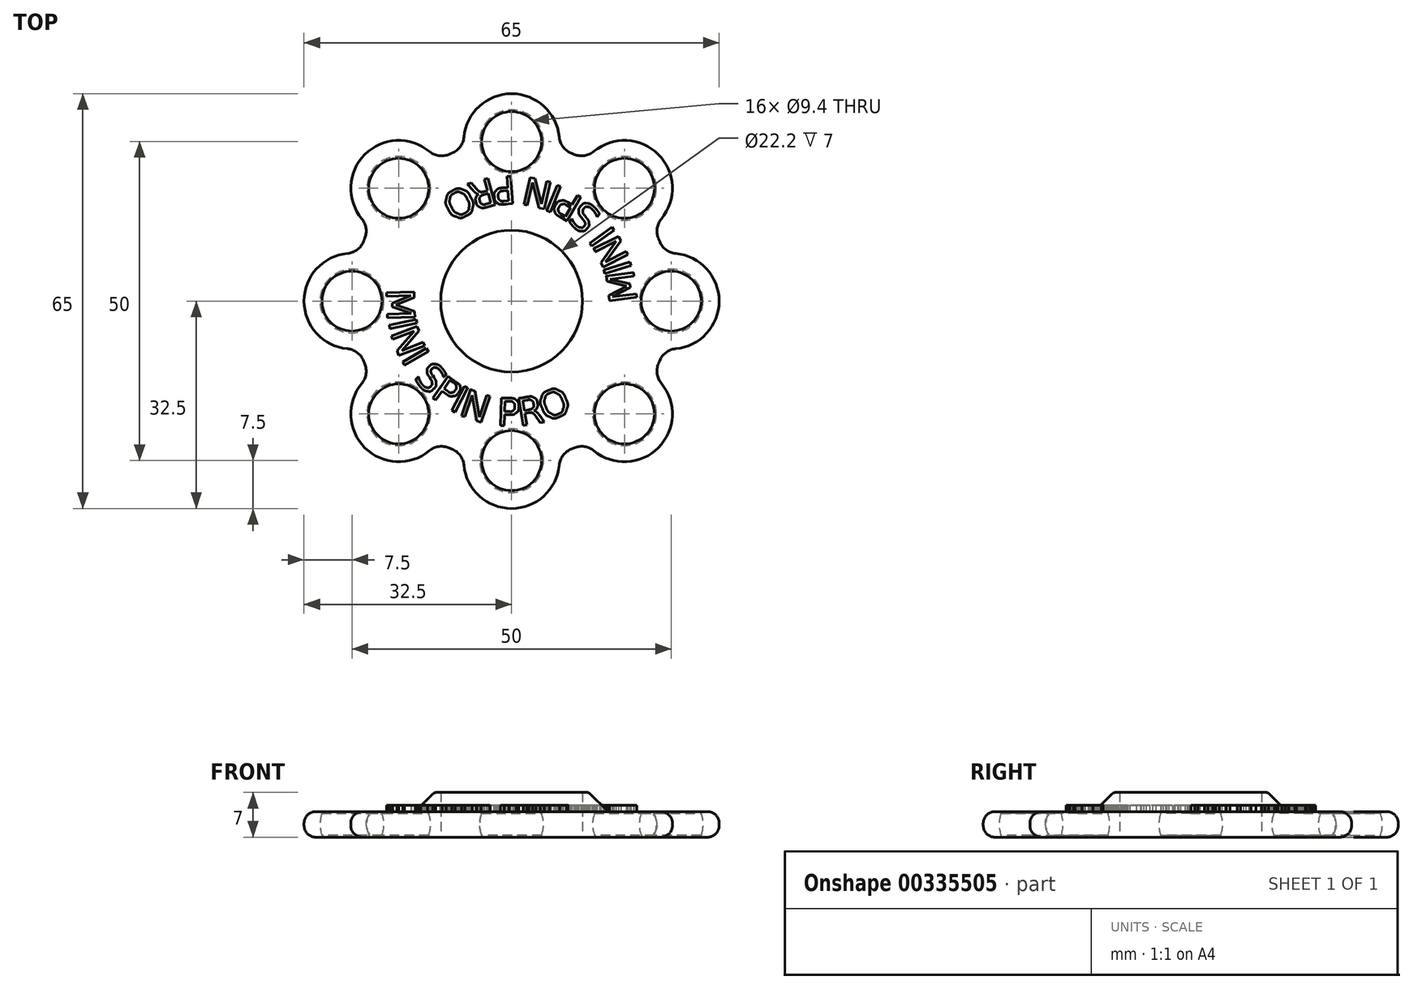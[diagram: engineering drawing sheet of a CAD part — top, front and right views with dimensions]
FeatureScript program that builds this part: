
annotation { "Feature Type Name" : "Feature", "Feature Type Description" : "" }
export const myFeature = defineFeature(function(context is Context, id is Id, definition is map)
    precondition{}
    {
        {
            var Q0;
            Q0=qCreatedBy(makeId("Top.planeOp"),FACE);
            var sketch = newSketch(context, id + "F0", { "sketchPlane" : qUnion([Q0])});
            skCircle(sketch, "E0", {"center": v(0, 0) * mm, "radius": 11.1 * mm});
            skPoint(sketch, "E1.0.midPoint", {"position": v(12.23, 6.82) * mm});
            skCircle(sketch, "E2", {"center": v(0, 25) * mm, "radius": 4.7 * mm});
            skCircle(sketch, "E3.1.0", {"center": v(-17.68, 17.68) * mm, "radius": 4.7 * mm});
            skCircle(sketch, "E3.2.0", {"center": v(-25, 0) * mm, "radius": 4.7 * mm});
            skCircle(sketch, "E3.3.0", {"center": v(-17.68, -17.68) * mm, "radius": 4.7 * mm});
            skCircle(sketch, "E3.4.0", {"center": v(0, -25) * mm, "radius": 4.7 * mm});
            skCircle(sketch, "E3.5.0", {"center": v(17.68, -17.68) * mm, "radius": 4.7 * mm});
            skCircle(sketch, "E3.6.0", {"center": v(25, 0) * mm, "radius": 4.7 * mm});
            skCircle(sketch, "E3.7.0", {"center": v(17.68, 17.68) * mm, "radius": 4.7 * mm});
            skCircle(sketch, "E4", {"center": v(0, 25) * mm, "radius": 7.5 * mm});
            skCircle(sketch, "E5.1.0", {"center": v(-17.68, 17.68) * mm, "radius": 7.5 * mm});
            skCircle(sketch, "E5.2.0", {"center": v(-25, 0) * mm, "radius": 7.5 * mm});
            skCircle(sketch, "E5.3.0", {"center": v(-17.68, -17.68) * mm, "radius": 7.5 * mm});
            skCircle(sketch, "E5.4.0", {"center": v(0, -25) * mm, "radius": 7.5 * mm});
            skCircle(sketch, "E5.5.0", {"center": v(17.68, -17.68) * mm, "radius": 7.5 * mm});
            skCircle(sketch, "E5.6.0", {"center": v(25, 0) * mm, "radius": 7.5 * mm});
            skCircle(sketch, "E5.7.0", {"center": v(17.68, 17.68) * mm, "radius": 7.5 * mm});
            skCircle(sketch, "E6", {"center": v(0, 0) * mm, "radius": 25 * mm});
            skSolve(sketch);
        }
        {
            var Q0;
            Q0=makeQuery(id+"F0.imprint","IMPRINT",FACE,{"disambiguationData":[TD([[makeQuery(id+"F0.imprint","IMPRINT",EDGE,{"derivedFrom":sQuery(id+"F0.wireOp",EDGE,"E0")}),-1.0]])]});
            var Q1;
            {var subQ0=sQuery(id+"F0.wireOp",EDGE,"E6");var subQ1=sQuery(id+"F0.wireOp",EDGE,"E3.3.0");var subQ2=makeQuery(id+"F0.imprint","INTERSECT",VERTEX,{"disambiguationData":[OD(0.0)],"derivedFrom":[subQ1,subQ0]});Q1=makeQuery(id+"F0.imprint","IMPRINT",FACE,{"disambiguationData":[TD([[makeQuery(id+"F0.imprint","IMPRINT",EDGE,{"disambiguationData":[TD([[subQ2,-1.0]])],"derivedFrom":subQ1}),-1.0]])]});}
            var Q2;
            {var subQ0=sQuery(id+"F0.wireOp",EDGE,"E6");var subQ1=sQuery(id+"F0.wireOp",EDGE,"E3.3.0");var subQ2=makeQuery(id+"F0.imprint","INTERSECT",VERTEX,{"disambiguationData":[OD(0.0)],"derivedFrom":[subQ1,subQ0]});Q2=makeQuery(id+"F0.imprint","IMPRINT",FACE,{"disambiguationData":[TD([[makeQuery(id+"F0.imprint","IMPRINT",EDGE,{"disambiguationData":[TD([[subQ2,1.0]])],"derivedFrom":subQ1}),-1.0]])]});}
            var Q3;
            {var subQ0=sQuery(id+"F0.wireOp",EDGE,"E6");var subQ1=sQuery(id+"F0.wireOp",EDGE,"E3.2.0");var subQ2=makeQuery(id+"F0.imprint","INTERSECT",VERTEX,{"disambiguationData":[OD(0.0)],"derivedFrom":[subQ1,subQ0]});Q3=makeQuery(id+"F0.imprint","IMPRINT",FACE,{"disambiguationData":[TD([[makeQuery(id+"F0.imprint","IMPRINT",EDGE,{"disambiguationData":[TD([[subQ2,1.0]])],"derivedFrom":subQ1}),-1.0]])]});}
            var Q4;
            {var subQ0=sQuery(id+"F0.wireOp",EDGE,"E6");var subQ1=sQuery(id+"F0.wireOp",EDGE,"E3.2.0");var subQ2=makeQuery(id+"F0.imprint","INTERSECT",VERTEX,{"disambiguationData":[OD(0.0)],"derivedFrom":[subQ1,subQ0]});Q4=makeQuery(id+"F0.imprint","IMPRINT",FACE,{"disambiguationData":[TD([[makeQuery(id+"F0.imprint","IMPRINT",EDGE,{"disambiguationData":[TD([[subQ2,-1.0]])],"derivedFrom":subQ1}),-1.0]])]});}
            var Q5;
            {var subQ0=sQuery(id+"F0.wireOp",EDGE,"E6");var subQ1=sQuery(id+"F0.wireOp",EDGE,"E3.1.0");var subQ2=makeQuery(id+"F0.imprint","INTERSECT",VERTEX,{"disambiguationData":[OD(0.0)],"derivedFrom":[subQ1,subQ0]});Q5=makeQuery(id+"F0.imprint","IMPRINT",FACE,{"disambiguationData":[TD([[makeQuery(id+"F0.imprint","IMPRINT",EDGE,{"disambiguationData":[TD([[subQ2,-1.0]])],"derivedFrom":subQ1}),-1.0]])]});}
            var Q6;
            {var subQ0=sQuery(id+"F0.wireOp",EDGE,"E6");var subQ1=sQuery(id+"F0.wireOp",EDGE,"E3.1.0");var subQ2=makeQuery(id+"F0.imprint","INTERSECT",VERTEX,{"disambiguationData":[OD(0.0)],"derivedFrom":[subQ1,subQ0]});Q6=makeQuery(id+"F0.imprint","IMPRINT",FACE,{"disambiguationData":[TD([[makeQuery(id+"F0.imprint","IMPRINT",EDGE,{"disambiguationData":[TD([[subQ2,1.0]])],"derivedFrom":subQ1}),-1.0]])]});}
            var Q7;
            {var subQ0=sQuery(id+"F0.wireOp",EDGE,"E6");var subQ1=sQuery(id+"F0.wireOp",EDGE,"E2");var subQ2=makeQuery(id+"F0.imprint","INTERSECT",VERTEX,{"disambiguationData":[OD(0.0)],"derivedFrom":[subQ1,subQ0]});Q7=makeQuery(id+"F0.imprint","IMPRINT",FACE,{"disambiguationData":[TD([[makeQuery(id+"F0.imprint","IMPRINT",EDGE,{"disambiguationData":[TD([[subQ2,1.0]])],"derivedFrom":subQ1}),-1.0]])]});}
            var Q8;
            {var subQ0=sQuery(id+"F0.wireOp",EDGE,"E6");var subQ1=sQuery(id+"F0.wireOp",EDGE,"E2");var subQ2=makeQuery(id+"F0.imprint","INTERSECT",VERTEX,{"disambiguationData":[OD(0.0)],"derivedFrom":[subQ1,subQ0]});Q8=makeQuery(id+"F0.imprint","IMPRINT",FACE,{"disambiguationData":[TD([[makeQuery(id+"F0.imprint","IMPRINT",EDGE,{"disambiguationData":[TD([[subQ2,-1.0]])],"derivedFrom":subQ1}),-1.0]])]});}
            var Q9;
            {var subQ0=sQuery(id+"F0.wireOp",EDGE,"E6");var subQ1=sQuery(id+"F0.wireOp",EDGE,"E3.7.0");var subQ2=makeQuery(id+"F0.imprint","INTERSECT",VERTEX,{"disambiguationData":[OD(0.0)],"derivedFrom":[subQ1,subQ0]});Q9=makeQuery(id+"F0.imprint","IMPRINT",FACE,{"disambiguationData":[TD([[makeQuery(id+"F0.imprint","IMPRINT",EDGE,{"disambiguationData":[TD([[subQ2,1.0]])],"derivedFrom":subQ1}),-1.0]])]});}
            var Q10;
            {var subQ0=sQuery(id+"F0.wireOp",EDGE,"E6");var subQ1=sQuery(id+"F0.wireOp",EDGE,"E3.7.0");var subQ2=makeQuery(id+"F0.imprint","INTERSECT",VERTEX,{"disambiguationData":[OD(0.0)],"derivedFrom":[subQ1,subQ0]});Q10=makeQuery(id+"F0.imprint","IMPRINT",FACE,{"disambiguationData":[TD([[makeQuery(id+"F0.imprint","IMPRINT",EDGE,{"disambiguationData":[TD([[subQ2,-1.0]])],"derivedFrom":subQ1}),-1.0]])]});}
            var Q11;
            {var subQ0=sQuery(id+"F0.wireOp",EDGE,"E6");var subQ1=sQuery(id+"F0.wireOp",EDGE,"E3.6.0");var subQ2=makeQuery(id+"F0.imprint","INTERSECT",VERTEX,{"disambiguationData":[OD(0.0)],"derivedFrom":[subQ1,subQ0]});Q11=makeQuery(id+"F0.imprint","IMPRINT",FACE,{"disambiguationData":[TD([[makeQuery(id+"F0.imprint","IMPRINT",EDGE,{"disambiguationData":[TD([[subQ2,-1.0]])],"derivedFrom":subQ1}),-1.0]])]});}
            var Q12;
            {var subQ0=sQuery(id+"F0.wireOp",EDGE,"E6");var subQ1=sQuery(id+"F0.wireOp",EDGE,"E3.6.0");var subQ2=makeQuery(id+"F0.imprint","INTERSECT",VERTEX,{"disambiguationData":[OD(0.0)],"derivedFrom":[subQ1,subQ0]});Q12=makeQuery(id+"F0.imprint","IMPRINT",FACE,{"disambiguationData":[TD([[makeQuery(id+"F0.imprint","IMPRINT",EDGE,{"disambiguationData":[TD([[subQ2,1.0]])],"derivedFrom":subQ1}),-1.0]])]});}
            var Q13;
            {var subQ0=sQuery(id+"F0.wireOp",EDGE,"E6");var subQ1=sQuery(id+"F0.wireOp",EDGE,"E3.5.0");var subQ2=makeQuery(id+"F0.imprint","INTERSECT",VERTEX,{"disambiguationData":[OD(0.0)],"derivedFrom":[subQ1,subQ0]});Q13=makeQuery(id+"F0.imprint","IMPRINT",FACE,{"disambiguationData":[TD([[makeQuery(id+"F0.imprint","IMPRINT",EDGE,{"disambiguationData":[TD([[subQ2,1.0]])],"derivedFrom":subQ1}),-1.0]])]});}
            var Q14;
            {var subQ0=sQuery(id+"F0.wireOp",EDGE,"E6");var subQ1=sQuery(id+"F0.wireOp",EDGE,"E3.5.0");var subQ2=makeQuery(id+"F0.imprint","INTERSECT",VERTEX,{"disambiguationData":[OD(0.0)],"derivedFrom":[subQ1,subQ0]});Q14=makeQuery(id+"F0.imprint","IMPRINT",FACE,{"disambiguationData":[TD([[makeQuery(id+"F0.imprint","IMPRINT",EDGE,{"disambiguationData":[TD([[subQ2,-1.0]])],"derivedFrom":subQ1}),-1.0]])]});}
            var Q15;
            {var subQ0=sQuery(id+"F0.wireOp",EDGE,"E6");var subQ1=sQuery(id+"F0.wireOp",EDGE,"E3.4.0");var subQ2=makeQuery(id+"F0.imprint","INTERSECT",VERTEX,{"disambiguationData":[OD(0.0)],"derivedFrom":[subQ1,subQ0]});Q15=makeQuery(id+"F0.imprint","IMPRINT",FACE,{"disambiguationData":[TD([[makeQuery(id+"F0.imprint","IMPRINT",EDGE,{"disambiguationData":[TD([[subQ2,1.0]])],"derivedFrom":subQ1}),-1.0]])]});}
            var Q16;
            {var subQ0=sQuery(id+"F0.wireOp",EDGE,"E6");var subQ1=sQuery(id+"F0.wireOp",EDGE,"E3.4.0");var subQ2=makeQuery(id+"F0.imprint","INTERSECT",VERTEX,{"disambiguationData":[OD(0.0)],"derivedFrom":[subQ1,subQ0]});Q16=makeQuery(id+"F0.imprint","IMPRINT",FACE,{"disambiguationData":[TD([[makeQuery(id+"F0.imprint","IMPRINT",EDGE,{"disambiguationData":[TD([[subQ2,-1.0]])],"derivedFrom":subQ1}),-1.0]])]});}
            extrude(context, id + "F1", {"entities" : qUnion([Q0, Q1, Q2, Q3, Q4, Q5, Q6, Q7, Q8, Q9, Q10, Q11, Q12, Q13, Q14, Q15, Q16]), "depth" : 2 * mm, "hasSecondDirection" : true, "secondDirectionOppositeDirection" : true, "secondDirectionDepth" : 2 * mm});
        }
        {
            var Q0;
            {var subQ0=sQuery(id+"F0.wireOp",EDGE,"E6");var subQ1=sQuery(id+"F0.wireOp",EDGE,"E5.4.0");Q0=makeQuery(id+"F1.opExtrude","SWEPT_EDGE",EDGE,{"disambiguationData":[OSD([subQ1,subQ0]),TDD([makeQuery(id+"F0.imprint","INTERSECT",VERTEX,{"disambiguationData":[OD(0.0)],"derivedFrom":[subQ1,subQ0]})])]});}
            var Q1;
            {var subQ0=sQuery(id+"F0.wireOp",EDGE,"E6");var subQ1=sQuery(id+"F0.wireOp",EDGE,"E5.2.0");Q1=makeQuery(id+"F1.opExtrude","SWEPT_EDGE",EDGE,{"disambiguationData":[OSD([subQ1,subQ0]),TDD([makeQuery(id+"F0.imprint","INTERSECT",VERTEX,{"disambiguationData":[OD(1.0)],"derivedFrom":[subQ1,subQ0]})])]});}
            var Q2;
            {var subQ0=sQuery(id+"F0.wireOp",EDGE,"E6");var subQ1=sQuery(id+"F0.wireOp",EDGE,"E5.2.0");Q2=makeQuery(id+"F1.opExtrude","SWEPT_EDGE",EDGE,{"disambiguationData":[OSD([subQ1,subQ0]),TDD([makeQuery(id+"F0.imprint","INTERSECT",VERTEX,{"disambiguationData":[OD(0.0)],"derivedFrom":[subQ1,subQ0]})])]});}
            var Q3;
            {var subQ0=sQuery(id+"F0.wireOp",EDGE,"E6");var subQ1=sQuery(id+"F0.wireOp",EDGE,"E4");Q3=makeQuery(id+"F1.opExtrude","SWEPT_EDGE",EDGE,{"disambiguationData":[OSD([subQ1,subQ0]),TDD([makeQuery(id+"F0.imprint","INTERSECT",VERTEX,{"disambiguationData":[OD(1.0)],"derivedFrom":[subQ1,subQ0]})])]});}
            var Q4;
            {var subQ0=sQuery(id+"F0.wireOp",EDGE,"E6");var subQ1=sQuery(id+"F0.wireOp",EDGE,"E5.7.0");Q4=makeQuery(id+"F1.opExtrude","SWEPT_EDGE",EDGE,{"disambiguationData":[OSD([subQ1,subQ0]),TDD([makeQuery(id+"F0.imprint","INTERSECT",VERTEX,{"disambiguationData":[OD(1.0)],"derivedFrom":[subQ1,subQ0]})])]});}
            var Q5;
            {var subQ0=sQuery(id+"F0.wireOp",EDGE,"E6");var subQ1=sQuery(id+"F0.wireOp",EDGE,"E5.1.0");Q5=makeQuery(id+"F1.opExtrude","SWEPT_EDGE",EDGE,{"disambiguationData":[OSD([subQ1,subQ0]),TDD([makeQuery(id+"F0.imprint","INTERSECT",VERTEX,{"disambiguationData":[OD(1.0)],"derivedFrom":[subQ1,subQ0]})])]});}
            var Q6;
            {var subQ0=sQuery(id+"F0.wireOp",EDGE,"E6");var subQ1=sQuery(id+"F0.wireOp",EDGE,"E5.3.0");Q6=makeQuery(id+"F1.opExtrude","SWEPT_EDGE",EDGE,{"disambiguationData":[OSD([subQ1,subQ0]),TDD([makeQuery(id+"F0.imprint","INTERSECT",VERTEX,{"disambiguationData":[OD(0.0)],"derivedFrom":[subQ1,subQ0]})])]});}
            var Q7;
            {var subQ0=sQuery(id+"F0.wireOp",EDGE,"E6");var subQ1=sQuery(id+"F0.wireOp",EDGE,"E5.1.0");Q7=makeQuery(id+"F1.opExtrude","SWEPT_EDGE",EDGE,{"disambiguationData":[OSD([subQ1,subQ0]),TDD([makeQuery(id+"F0.imprint","INTERSECT",VERTEX,{"disambiguationData":[OD(0.0)],"derivedFrom":[subQ1,subQ0]})])]});}
            var Q8;
            {var subQ0=sQuery(id+"F0.wireOp",EDGE,"E6");var subQ1=sQuery(id+"F0.wireOp",EDGE,"E4");Q8=makeQuery(id+"F1.opExtrude","SWEPT_EDGE",EDGE,{"disambiguationData":[OSD([subQ1,subQ0]),TDD([makeQuery(id+"F0.imprint","INTERSECT",VERTEX,{"disambiguationData":[OD(0.0)],"derivedFrom":[subQ1,subQ0]})])]});}
            var Q9;
            {var subQ0=sQuery(id+"F0.wireOp",EDGE,"E6");var subQ1=sQuery(id+"F0.wireOp",EDGE,"E5.6.0");Q9=makeQuery(id+"F1.opExtrude","SWEPT_EDGE",EDGE,{"disambiguationData":[OSD([subQ1,subQ0]),TDD([makeQuery(id+"F0.imprint","INTERSECT",VERTEX,{"disambiguationData":[OD(0.0)],"derivedFrom":[subQ1,subQ0]})])]});}
            var Q10;
            {var subQ0=sQuery(id+"F0.wireOp",EDGE,"E6");var subQ1=sQuery(id+"F0.wireOp",EDGE,"E5.7.0");Q10=makeQuery(id+"F1.opExtrude","SWEPT_EDGE",EDGE,{"disambiguationData":[OSD([subQ1,subQ0]),TDD([makeQuery(id+"F0.imprint","INTERSECT",VERTEX,{"disambiguationData":[OD(0.0)],"derivedFrom":[subQ1,subQ0]})])]});}
            var Q11;
            {var subQ0=sQuery(id+"F0.wireOp",EDGE,"E6");var subQ1=sQuery(id+"F0.wireOp",EDGE,"E5.6.0");Q11=makeQuery(id+"F1.opExtrude","SWEPT_EDGE",EDGE,{"disambiguationData":[OSD([subQ1,subQ0]),TDD([makeQuery(id+"F0.imprint","INTERSECT",VERTEX,{"disambiguationData":[OD(1.0)],"derivedFrom":[subQ1,subQ0]})])]});}
            var Q12;
            {var subQ0=sQuery(id+"F0.wireOp",EDGE,"E6");var subQ1=sQuery(id+"F0.wireOp",EDGE,"E5.5.0");Q12=makeQuery(id+"F1.opExtrude","SWEPT_EDGE",EDGE,{"disambiguationData":[OSD([subQ1,subQ0]),TDD([makeQuery(id+"F0.imprint","INTERSECT",VERTEX,{"disambiguationData":[OD(1.0)],"derivedFrom":[subQ1,subQ0]})])]});}
            var Q13;
            {var subQ0=sQuery(id+"F0.wireOp",EDGE,"E6");var subQ1=sQuery(id+"F0.wireOp",EDGE,"E5.5.0");Q13=makeQuery(id+"F1.opExtrude","SWEPT_EDGE",EDGE,{"disambiguationData":[OSD([subQ1,subQ0]),TDD([makeQuery(id+"F0.imprint","INTERSECT",VERTEX,{"disambiguationData":[OD(0.0)],"derivedFrom":[subQ1,subQ0]})])]});}
            var Q14;
            {var subQ0=sQuery(id+"F0.wireOp",EDGE,"E6");var subQ1=sQuery(id+"F0.wireOp",EDGE,"E5.4.0");Q14=makeQuery(id+"F1.opExtrude","SWEPT_EDGE",EDGE,{"disambiguationData":[OSD([subQ1,subQ0]),TDD([makeQuery(id+"F0.imprint","INTERSECT",VERTEX,{"disambiguationData":[OD(1.0)],"derivedFrom":[subQ1,subQ0]})])]});}
            var Q15;
            {var subQ0=sQuery(id+"F0.wireOp",EDGE,"E6");var subQ1=sQuery(id+"F0.wireOp",EDGE,"E5.3.0");Q15=makeQuery(id+"F1.opExtrude","SWEPT_EDGE",EDGE,{"disambiguationData":[OSD([subQ1,subQ0]),TDD([makeQuery(id+"F0.imprint","INTERSECT",VERTEX,{"disambiguationData":[OD(1.0)],"derivedFrom":[subQ1,subQ0]})])]});}
            fillet(context, id + "F2", {"entities" : qUnion([Q0, Q1, Q2, Q3, Q4, Q5, Q6, Q7, Q8, Q9, Q10, Q11, Q12, Q13, Q14, Q15]), "radius" : 3 * mm, "tangentPropagation" : true, "allowEdgeOverflow" : false});
        }
        {
            var Q0;
            Q0=makeQuery(id+"F1.opExtrude","CAP_EDGE",EDGE,{"disambiguationData":[OSD([sQuery(id+"F0.wireOp",EDGE,"E5.7.0")])],"isStart":false});
            var Q1;
            Q1=makeQuery(id+"F1.opExtrude","CAP_EDGE",EDGE,{"disambiguationData":[OSD([sQuery(id+"F0.wireOp",EDGE,"E5.7.0")])],"isStart":true});
            fillet(context, id + "F3", {"entities" : qUnion([Q0, Q1]), "radius" : 1.8 * mm, "tangentPropagation" : true, "allowEdgeOverflow" : false});
        }
        {
            var Q0;
            Q0=qCreatedBy(makeId("Right.planeOp"),FACE);
            var sketch = newSketch(context, id + "F4", { "sketchPlane" : qUnion([Q0])});
            skPoint(sketch, "E7.0", {"position": v(-25, 0) * mm});
            skPoint(sketch, "E7.1", {"position": v(25, 0) * mm});
            skLineSegment(sketch, "E8", {"start": v(-25, 12.35) * mm, "end": v(-25, -14.21) * mm, "construction": true});
            skLineSegment(sketch, "E9", {"start": v(25, 12.16) * mm, "end": v(25, -14.21) * mm, "construction": true});
            skPoint(sketch, "E10", {"position": v(-25, 5) * mm});
            skPoint(sketch, "E11", {"position": v(-25, -5) * mm});
            skPoint(sketch, "E12", {"position": v(25, 5) * mm});
            skPoint(sketch, "E13", {"position": v(25, -5) * mm});
            skArc(sketch, "E14", {"start": v(-25, 5) * mm, "mid": v(-30, 0) * mm, "end": v(-25, -5) * mm});
            skArc(sketch, "E15", {"start": v(25, -5) * mm, "mid": v(30, 0) * mm, "end": v(25, 5) * mm});
            skLineSegment(sketch, "E16", {"start": v(-25, 5) * mm, "end": v(-25, -5) * mm});
            skLineSegment(sketch, "E17", {"start": v(25, 5) * mm, "end": v(25, -5) * mm});
            skLineSegment(sketch, "E18", {"start": v(0, 41.23) * mm, "end": v(0, -49.38) * mm, "construction": true});
            skSolve(sketch);
        }
        {
            var Q0;
            Q0=makeQuery(id+"F4.imprint","IMPRINT",FACE,{"disambiguationData":[TD([[makeQuery(id+"F4.imprint","IMPRINT",EDGE,{"derivedFrom":sQuery(id+"F4.wireOp",EDGE,"E14")}),1.0]])]});
            var Q1;
            Q1=sQuery(id+"F4.wireOp",EDGE,"E8");
            revolve(context, id + "F5", {"entities" : qUnion([Q0]), "axis" : qUnion([Q1]), "revolveType" : RevolveType.FULL});
        }
        {
            var Q0;
            Q0=makeQuery(id+"F4.imprint","IMPRINT",FACE,{"disambiguationData":[TD([[makeQuery(id+"F4.imprint","IMPRINT",EDGE,{"derivedFrom":sQuery(id+"F4.wireOp",EDGE,"E15")}),1.0]])]});
            var Q1;
            Q1=sQuery(id+"F4.wireOp",EDGE,"E9");
            revolve(context, id + "F6", {"entities" : qUnion([Q0]), "axis" : qUnion([Q1]), "revolveType" : RevolveType.FULL});
        }
        {
            var Q0;
            Q0=makeQuery(id+"F6.opRevolve","SWEPT_BODY",BODY,{"disambiguationData":[OSD([sQuery(id+"F4.wireOp",EDGE,"E15"),sQuery(id+"F4.wireOp",EDGE,"E17")])]});
            var Q1;
            Q1=makeQuery(id+"F5.opRevolve","SWEPT_BODY",BODY,{"disambiguationData":[OSD([sQuery(id+"F4.wireOp",EDGE,"E14"),sQuery(id+"F4.wireOp",EDGE,"E16")])]});
            var Q2;
            Q2=makeQuery(id+"F1.opExtrude","SWEPT_BODY",BODY,{"disambiguationData":[OSD([sQuery(id+"F0.wireOp",EDGE,"E0"),sQuery(id+"F0.wireOp",EDGE,"E2"),sQuery(id+"F0.wireOp",EDGE,"E3.1.0"),sQuery(id+"F0.wireOp",EDGE,"E3.2.0"),sQuery(id+"F0.wireOp",EDGE,"E3.3.0"),sQuery(id+"F0.wireOp",EDGE,"E3.4.0"),sQuery(id+"F0.wireOp",EDGE,"E3.5.0"),sQuery(id+"F0.wireOp",EDGE,"E3.6.0"),sQuery(id+"F0.wireOp",EDGE,"E3.7.0"),sQuery(id+"F0.wireOp",EDGE,"E4"),sQuery(id+"F0.wireOp",EDGE,"E5.1.0"),sQuery(id+"F0.wireOp",EDGE,"E5.2.0"),sQuery(id+"F0.wireOp",EDGE,"E5.3.0"),sQuery(id+"F0.wireOp",EDGE,"E5.4.0"),sQuery(id+"F0.wireOp",EDGE,"E5.5.0"),sQuery(id+"F0.wireOp",EDGE,"E5.6.0"),sQuery(id+"F0.wireOp",EDGE,"E5.7.0"),sQuery(id+"F0.wireOp",EDGE,"E6")])]});
            booleanBodies(context, id + "F7", {"operationType" : BooleanOperationType.SUBTRACTION, "tools" : qUnion([Q0, Q1]), "targets" : qUnion([Q2])});
        }
        {
            var Q0;
            Q0=qCreatedBy(makeId("Front.planeOp"),FACE);
            var sketch = newSketch(context, id + "F8", { "sketchPlane" : qUnion([Q0])});
            skPoint(sketch, "E19.0", {"position": v(-25, 0) * mm});
            skPoint(sketch, "E19.1", {"position": v(25, 0) * mm});
            skLineSegment(sketch, "E20", {"start": v(-25, 18.9) * mm, "end": v(-25, -20.91) * mm, "construction": true});
            skLineSegment(sketch, "E21", {"start": v(25, 20.02) * mm, "end": v(25, -22.02) * mm, "construction": true});
            skPoint(sketch, "E22", {"position": v(-25, 5) * mm});
            skPoint(sketch, "E23", {"position": v(-25, -5) * mm});
            skPoint(sketch, "E24", {"position": v(25, 5) * mm});
            skPoint(sketch, "E25", {"position": v(25, -5) * mm});
            skArc(sketch, "E26", {"start": v(-25, 5) * mm, "mid": v(-30, 0) * mm, "end": v(-25, -5) * mm});
            skArc(sketch, "E27", {"start": v(25, -5) * mm, "mid": v(30, 0) * mm, "end": v(25, 5) * mm});
            skLineSegment(sketch, "E28", {"start": v(-25, 5) * mm, "end": v(-25, -5) * mm});
            skLineSegment(sketch, "E29", {"start": v(25, 5) * mm, "end": v(25, -5) * mm});
            skSolve(sketch);
        }
        {
            var Q0;
            Q0=makeQuery(id+"F8.imprint","IMPRINT",FACE,{"disambiguationData":[TD([[makeQuery(id+"F8.imprint","IMPRINT",EDGE,{"derivedFrom":sQuery(id+"F8.wireOp",EDGE,"E26")}),1.0]])]});
            var Q1;
            Q1=sQuery(id+"F8.wireOp",EDGE,"E20");
            revolve(context, id + "F9", {"entities" : qUnion([Q0]), "axis" : qUnion([Q1]), "revolveType" : RevolveType.FULL});
        }
        {
            var Q0;
            Q0=makeQuery(id+"F8.imprint","IMPRINT",FACE,{"disambiguationData":[TD([[makeQuery(id+"F8.imprint","IMPRINT",EDGE,{"derivedFrom":sQuery(id+"F8.wireOp",EDGE,"E27")}),1.0]])]});
            var Q1;
            Q1=sQuery(id+"F8.wireOp",EDGE,"E21");
            revolve(context, id + "F10", {"entities" : qUnion([Q0]), "axis" : qUnion([Q1]), "revolveType" : RevolveType.FULL});
        }
        {
            var Q0;
            Q0=makeQuery(id+"F9.opRevolve","SWEPT_BODY",BODY,{"disambiguationData":[OSD([sQuery(id+"F8.wireOp",EDGE,"E26"),sQuery(id+"F8.wireOp",EDGE,"E28")])]});
            var Q1;
            Q1=makeQuery(id+"F10.opRevolve","SWEPT_BODY",BODY,{"disambiguationData":[OSD([sQuery(id+"F8.wireOp",EDGE,"E27"),sQuery(id+"F8.wireOp",EDGE,"E29")])]});
            var Q2;
            Q2=makeQuery(id+"F1.opExtrude","SWEPT_BODY",BODY,{"disambiguationData":[OSD([sQuery(id+"F0.wireOp",EDGE,"E0"),sQuery(id+"F0.wireOp",EDGE,"E2"),sQuery(id+"F0.wireOp",EDGE,"E3.1.0"),sQuery(id+"F0.wireOp",EDGE,"E3.2.0"),sQuery(id+"F0.wireOp",EDGE,"E3.3.0"),sQuery(id+"F0.wireOp",EDGE,"E3.4.0"),sQuery(id+"F0.wireOp",EDGE,"E3.5.0"),sQuery(id+"F0.wireOp",EDGE,"E3.6.0"),sQuery(id+"F0.wireOp",EDGE,"E3.7.0"),sQuery(id+"F0.wireOp",EDGE,"E4"),sQuery(id+"F0.wireOp",EDGE,"E5.1.0"),sQuery(id+"F0.wireOp",EDGE,"E5.2.0"),sQuery(id+"F0.wireOp",EDGE,"E5.3.0"),sQuery(id+"F0.wireOp",EDGE,"E5.4.0"),sQuery(id+"F0.wireOp",EDGE,"E5.5.0"),sQuery(id+"F0.wireOp",EDGE,"E5.6.0"),sQuery(id+"F0.wireOp",EDGE,"E5.7.0"),sQuery(id+"F0.wireOp",EDGE,"E6")])]});
            booleanBodies(context, id + "F11", {"operationType" : BooleanOperationType.SUBTRACTION, "tools" : qUnion([Q0, Q1]), "targets" : qUnion([Q2])});
        }
        {
            var Q0;
            Q0=qCreatedBy(makeId("Front.planeOp"),FACE);
            var Q1;
            Q1=sQuery(id+"F0.wireOp",VERTEX,"E3.3.0.center");
            cPlane(context, id + "F12", {"entities" : qUnion([Q0, Q1]), "cplaneType" : CPlaneType.PLANE_POINT, "offset" : 25 * mm, "width" : 150 * mm, "height" : 150 * mm});
        }
        {
            var Q0;
            Q0=qCreatedBy(id+"F12.planeOp",FACE);
            var sketch = newSketch(context, id + "F13", { "sketchPlane" : qUnion([Q0])});
            skPoint(sketch, "E30.0", {"position": v(-17.68, 0) * mm});
            skPoint(sketch, "E30.1", {"position": v(17.68, 0) * mm});
            skLineSegment(sketch, "E31", {"start": v(-17.68, 20.76) * mm, "end": v(-17.68, -25.8) * mm, "construction": true});
            skLineSegment(sketch, "E32", {"start": v(17.68, 18.25) * mm, "end": v(17.68, -22.97) * mm, "construction": true});
            skPoint(sketch, "E33", {"position": v(-17.68, 5) * mm});
            skPoint(sketch, "E34", {"position": v(-17.68, -5) * mm});
            skPoint(sketch, "E35", {"position": v(17.68, -5) * mm});
            skPoint(sketch, "E36", {"position": v(17.68, 5) * mm});
            skArc(sketch, "E37", {"start": v(-17.68, 5) * mm, "mid": v(-22.68, 0) * mm, "end": v(-17.68, -5) * mm});
            skArc(sketch, "E38", {"start": v(17.68, -5) * mm, "mid": v(22.68, 0) * mm, "end": v(17.68, 5) * mm});
            skLineSegment(sketch, "E39", {"start": v(-17.68, 5) * mm, "end": v(-17.68, -5) * mm});
            skLineSegment(sketch, "E40", {"start": v(17.68, 5) * mm, "end": v(17.68, -5) * mm});
            skSolve(sketch);
        }
        {
            var Q0;
            Q0=makeQuery(id+"F13.imprint","IMPRINT",FACE,{"disambiguationData":[TD([[makeQuery(id+"F13.imprint","IMPRINT",EDGE,{"derivedFrom":sQuery(id+"F13.wireOp",EDGE,"E37")}),1.0]])]});
            var Q1;
            Q1=sQuery(id+"F13.wireOp",EDGE,"E31");
            revolve(context, id + "F14", {"entities" : qUnion([Q0]), "axis" : qUnion([Q1]), "revolveType" : RevolveType.FULL});
        }
        {
            var Q0;
            Q0=makeQuery(id+"F13.imprint","IMPRINT",FACE,{"disambiguationData":[TD([[makeQuery(id+"F13.imprint","IMPRINT",EDGE,{"derivedFrom":sQuery(id+"F13.wireOp",EDGE,"E38")}),1.0]])]});
            var Q1;
            Q1=sQuery(id+"F13.wireOp",EDGE,"E32");
            revolve(context, id + "F15", {"entities" : qUnion([Q0]), "axis" : qUnion([Q1]), "revolveType" : RevolveType.FULL});
        }
        {
            var Q0;
            Q0=makeQuery(id+"F15.opRevolve","SWEPT_BODY",BODY,{"disambiguationData":[OSD([sQuery(id+"F13.wireOp",EDGE,"E38"),sQuery(id+"F13.wireOp",EDGE,"E40")])]});
            var Q1;
            Q1=makeQuery(id+"F14.opRevolve","SWEPT_BODY",BODY,{"disambiguationData":[OSD([sQuery(id+"F13.wireOp",EDGE,"E37"),sQuery(id+"F13.wireOp",EDGE,"E39")])]});
            var Q2;
            Q2=makeQuery(id+"F1.opExtrude","SWEPT_BODY",BODY,{"disambiguationData":[OSD([sQuery(id+"F0.wireOp",EDGE,"E0"),sQuery(id+"F0.wireOp",EDGE,"E2"),sQuery(id+"F0.wireOp",EDGE,"E3.1.0"),sQuery(id+"F0.wireOp",EDGE,"E3.2.0"),sQuery(id+"F0.wireOp",EDGE,"E3.3.0"),sQuery(id+"F0.wireOp",EDGE,"E3.4.0"),sQuery(id+"F0.wireOp",EDGE,"E3.5.0"),sQuery(id+"F0.wireOp",EDGE,"E3.6.0"),sQuery(id+"F0.wireOp",EDGE,"E3.7.0"),sQuery(id+"F0.wireOp",EDGE,"E4"),sQuery(id+"F0.wireOp",EDGE,"E5.1.0"),sQuery(id+"F0.wireOp",EDGE,"E5.2.0"),sQuery(id+"F0.wireOp",EDGE,"E5.3.0"),sQuery(id+"F0.wireOp",EDGE,"E5.4.0"),sQuery(id+"F0.wireOp",EDGE,"E5.5.0"),sQuery(id+"F0.wireOp",EDGE,"E5.6.0"),sQuery(id+"F0.wireOp",EDGE,"E5.7.0"),sQuery(id+"F0.wireOp",EDGE,"E6")])]});
            booleanBodies(context, id + "F16", {"operationType" : BooleanOperationType.SUBTRACTION, "tools" : qUnion([Q0, Q1]), "targets" : qUnion([Q2])});
        }
        {
            var Q0;
            Q0=qCreatedBy(makeId("Front.planeOp"),FACE);
            var Q1;
            Q1=sQuery(id+"F0.wireOp",VERTEX,"E5.7.0.center");
            cPlane(context, id + "F17", {"entities" : qUnion([Q0, Q1]), "cplaneType" : CPlaneType.PLANE_POINT, "offset" : 25 * mm, "width" : 150 * mm, "height" : 150 * mm});
        }
        {
            var Q0;
            Q0=qCreatedBy(id+"F17.planeOp",FACE);
            var sketch = newSketch(context, id + "F18", { "sketchPlane" : qUnion([Q0])});
            skPoint(sketch, "E41.0", {"position": v(17.68, 0) * mm});
            skPoint(sketch, "E41.1", {"position": v(-17.68, 0) * mm});
            skLineSegment(sketch, "E42", {"start": v(17.68, 20.69) * mm, "end": v(17.68, -19.13) * mm, "construction": true});
            skLineSegment(sketch, "E43", {"start": v(-17.68, 22.25) * mm, "end": v(-17.68, -19.13) * mm, "construction": true});
            skPoint(sketch, "E44", {"position": v(17.68, 5) * mm});
            skPoint(sketch, "E45", {"position": v(-17.68, 5) * mm});
            skPoint(sketch, "E46", {"position": v(17.68, -5) * mm});
            skPoint(sketch, "E47", {"position": v(-17.68, -5) * mm});
            skArc(sketch, "E48", {"start": v(17.68, -5) * mm, "mid": v(22.68, 0) * mm, "end": v(17.68, 5) * mm});
            skArc(sketch, "E49", {"start": v(-17.68, 5) * mm, "mid": v(-22.68, 0) * mm, "end": v(-17.68, -5) * mm});
            skLineSegment(sketch, "E50", {"start": v(17.68, 5) * mm, "end": v(17.68, -5) * mm});
            skLineSegment(sketch, "E51", {"start": v(-17.68, 5) * mm, "end": v(-17.68, -5) * mm});
            skSolve(sketch);
        }
        {
            var Q0;
            Q0=makeQuery(id+"F18.imprint","IMPRINT",FACE,{"disambiguationData":[TD([[makeQuery(id+"F18.imprint","IMPRINT",EDGE,{"derivedFrom":sQuery(id+"F18.wireOp",EDGE,"E48")}),1.0]])]});
            var Q1;
            Q1=sQuery(id+"F18.wireOp",EDGE,"E42");
            revolve(context, id + "F19", {"entities" : qUnion([Q0]), "axis" : qUnion([Q1]), "revolveType" : RevolveType.FULL});
        }
        {
            var Q0;
            Q0=makeQuery(id+"F18.imprint","IMPRINT",FACE,{"disambiguationData":[TD([[makeQuery(id+"F18.imprint","IMPRINT",EDGE,{"derivedFrom":sQuery(id+"F18.wireOp",EDGE,"E49")}),1.0]])]});
            var Q1;
            Q1=sQuery(id+"F18.wireOp",EDGE,"E43");
            revolve(context, id + "F20", {"entities" : qUnion([Q0]), "axis" : qUnion([Q1]), "revolveType" : RevolveType.FULL});
        }
        {
            var Q0;
            Q0=makeQuery(id+"F20.opRevolve","SWEPT_BODY",BODY,{"disambiguationData":[OSD([sQuery(id+"F18.wireOp",EDGE,"E49"),sQuery(id+"F18.wireOp",EDGE,"E51")])]});
            var Q1;
            Q1=makeQuery(id+"F19.opRevolve","SWEPT_BODY",BODY,{"disambiguationData":[OSD([sQuery(id+"F18.wireOp",EDGE,"E48"),sQuery(id+"F18.wireOp",EDGE,"E50")])]});
            var Q2;
            Q2=makeQuery(id+"F1.opExtrude","SWEPT_BODY",BODY,{"disambiguationData":[OSD([sQuery(id+"F0.wireOp",EDGE,"E0"),sQuery(id+"F0.wireOp",EDGE,"E2"),sQuery(id+"F0.wireOp",EDGE,"E3.1.0"),sQuery(id+"F0.wireOp",EDGE,"E3.2.0"),sQuery(id+"F0.wireOp",EDGE,"E3.3.0"),sQuery(id+"F0.wireOp",EDGE,"E3.4.0"),sQuery(id+"F0.wireOp",EDGE,"E3.5.0"),sQuery(id+"F0.wireOp",EDGE,"E3.6.0"),sQuery(id+"F0.wireOp",EDGE,"E3.7.0"),sQuery(id+"F0.wireOp",EDGE,"E4"),sQuery(id+"F0.wireOp",EDGE,"E5.1.0"),sQuery(id+"F0.wireOp",EDGE,"E5.2.0"),sQuery(id+"F0.wireOp",EDGE,"E5.3.0"),sQuery(id+"F0.wireOp",EDGE,"E5.4.0"),sQuery(id+"F0.wireOp",EDGE,"E5.5.0"),sQuery(id+"F0.wireOp",EDGE,"E5.6.0"),sQuery(id+"F0.wireOp",EDGE,"E5.7.0"),sQuery(id+"F0.wireOp",EDGE,"E6")])]});
            booleanBodies(context, id + "F21", {"operationType" : BooleanOperationType.SUBTRACTION, "tools" : qUnion([Q0, Q1]), "targets" : qUnion([Q2])});
        }
        {
            var Q0;
            Q0=makeQuery(id+"F1.opExtrude","CAP_FACE",FACE,{"disambiguationData":[OSD([sQuery(id+"F0.wireOp",EDGE,"E0"),sQuery(id+"F0.wireOp",EDGE,"E2"),sQuery(id+"F0.wireOp",EDGE,"E3.1.0"),sQuery(id+"F0.wireOp",EDGE,"E3.2.0"),sQuery(id+"F0.wireOp",EDGE,"E3.3.0"),sQuery(id+"F0.wireOp",EDGE,"E3.4.0"),sQuery(id+"F0.wireOp",EDGE,"E3.5.0"),sQuery(id+"F0.wireOp",EDGE,"E3.6.0"),sQuery(id+"F0.wireOp",EDGE,"E3.7.0"),sQuery(id+"F0.wireOp",EDGE,"E4"),sQuery(id+"F0.wireOp",EDGE,"E5.1.0"),sQuery(id+"F0.wireOp",EDGE,"E5.2.0"),sQuery(id+"F0.wireOp",EDGE,"E5.3.0"),sQuery(id+"F0.wireOp",EDGE,"E5.4.0"),sQuery(id+"F0.wireOp",EDGE,"E5.5.0"),sQuery(id+"F0.wireOp",EDGE,"E5.6.0"),sQuery(id+"F0.wireOp",EDGE,"E5.7.0"),sQuery(id+"F0.wireOp",EDGE,"E6")])],"isStart":false});
            var sketch = newSketch(context, id + "F22", { "sketchPlane" : qUnion([Q0])});
            skCircle(sketch, "E52.0", {"center": v(0, 0) * mm, "radius": 11.1 * mm});
            skCircle(sketch, "E53.0", {"center": v(0, 0) * mm, "radius": 15.1 * mm});
            skSolve(sketch);
        }
        {
            var Q0;
            Q0=makeQuery(id+"F22.imprint","IMPRINT",FACE,{"disambiguationData":[TD([[makeQuery(id+"F22.imprint","IMPRINT",EDGE,{"derivedFrom":sQuery(id+"F22.wireOp",EDGE,"E52.0")}),-1.0]])]});
            extrude(context, id + "F23", {"entities" : qUnion([Q0]), "operationType" : NewBodyOperationType.ADD, "depth" : 3 * mm});
        }
        {
            var Q0;
            Q0=makeQuery(id+"F23.opExtrude","CAP_EDGE",EDGE,{"disambiguationData":[OSD([sQuery(id+"F22.wireOp",EDGE,"E53.0")])],"isStart":false});
            chamfer(context, id + "F24", {"entities" : qUnion([Q0]), "width" : 3 * mm, "tangentPropagation" : true});
        }
        {
            var Q0;
            Q0=makeQuery(id+"F24.opChamfer","BLEND_EDGE",EDGE,{"blendedFrom":[makeQuery(id+"F23.opExtrude","CAP_EDGE",EDGE,{"disambiguationData":[OSD([sQuery(id+"F22.wireOp",EDGE,"E53.0")])],"isStart":false}),makeQuery(id+"F1.opExtrude","CAP_FACE",FACE,{"disambiguationData":[OSD([sQuery(id+"F0.wireOp",EDGE,"E0"),sQuery(id+"F0.wireOp",EDGE,"E2"),sQuery(id+"F0.wireOp",EDGE,"E3.1.0"),sQuery(id+"F0.wireOp",EDGE,"E3.2.0"),sQuery(id+"F0.wireOp",EDGE,"E3.3.0"),sQuery(id+"F0.wireOp",EDGE,"E3.4.0"),sQuery(id+"F0.wireOp",EDGE,"E3.5.0"),sQuery(id+"F0.wireOp",EDGE,"E3.6.0"),sQuery(id+"F0.wireOp",EDGE,"E3.7.0"),sQuery(id+"F0.wireOp",EDGE,"E4"),sQuery(id+"F0.wireOp",EDGE,"E5.1.0"),sQuery(id+"F0.wireOp",EDGE,"E5.2.0"),sQuery(id+"F0.wireOp",EDGE,"E5.3.0"),sQuery(id+"F0.wireOp",EDGE,"E5.4.0"),sQuery(id+"F0.wireOp",EDGE,"E5.5.0"),sQuery(id+"F0.wireOp",EDGE,"E5.6.0"),sQuery(id+"F0.wireOp",EDGE,"E5.7.0"),sQuery(id+"F0.wireOp",EDGE,"E6")])],"isStart":false})],"blendedInto":[makeQuery(id+"F1.opExtrude","CAP_FACE",FACE,{"disambiguationData":[OSD([sQuery(id+"F0.wireOp",EDGE,"E0"),sQuery(id+"F0.wireOp",EDGE,"E2"),sQuery(id+"F0.wireOp",EDGE,"E3.1.0"),sQuery(id+"F0.wireOp",EDGE,"E3.2.0"),sQuery(id+"F0.wireOp",EDGE,"E3.3.0"),sQuery(id+"F0.wireOp",EDGE,"E3.4.0"),sQuery(id+"F0.wireOp",EDGE,"E3.5.0"),sQuery(id+"F0.wireOp",EDGE,"E3.6.0"),sQuery(id+"F0.wireOp",EDGE,"E3.7.0"),sQuery(id+"F0.wireOp",EDGE,"E4"),sQuery(id+"F0.wireOp",EDGE,"E5.1.0"),sQuery(id+"F0.wireOp",EDGE,"E5.2.0"),sQuery(id+"F0.wireOp",EDGE,"E5.3.0"),sQuery(id+"F0.wireOp",EDGE,"E5.4.0"),sQuery(id+"F0.wireOp",EDGE,"E5.5.0"),sQuery(id+"F0.wireOp",EDGE,"E5.6.0"),sQuery(id+"F0.wireOp",EDGE,"E5.7.0"),sQuery(id+"F0.wireOp",EDGE,"E6")])],"isStart":false})]});
            var Q1;
            {var subQ0=sQuery(id+"F22.wireOp",EDGE,"E53.0");Q1=makeQuery(id+"F24.opChamfer","BLEND_EDGE",EDGE,{"blendedFrom":[makeQuery(id+"F23.opExtrude","CAP_EDGE",EDGE,{"disambiguationData":[OSD([subQ0])],"isStart":false}),makeQuery(id+"F23.opExtrude","CAP_FACE",FACE,{"disambiguationData":[OSD([sQuery(id+"F22.wireOp",EDGE,"E52.0"),subQ0])],"isStart":false})],"blendedInto":[makeQuery(id+"F23.opExtrude","CAP_FACE",FACE,{"disambiguationData":[OSD([sQuery(id+"F22.wireOp",EDGE,"E52.0"),subQ0])],"isStart":false})]});}
            fillet(context, id + "F25", {"entities" : qUnion([Q0, Q1]), "radius" : .75 * mm, "tangentPropagation" : true, "allowEdgeOverflow" : false});
        }
        {
            var Q0;
            Q0=makeQuery(id+"F1.opExtrude","CAP_FACE",FACE,{"disambiguationData":[OSD([sQuery(id+"F0.wireOp",EDGE,"E0"),sQuery(id+"F0.wireOp",EDGE,"E2"),sQuery(id+"F0.wireOp",EDGE,"E3.1.0"),sQuery(id+"F0.wireOp",EDGE,"E3.2.0"),sQuery(id+"F0.wireOp",EDGE,"E3.3.0"),sQuery(id+"F0.wireOp",EDGE,"E3.4.0"),sQuery(id+"F0.wireOp",EDGE,"E3.5.0"),sQuery(id+"F0.wireOp",EDGE,"E3.6.0"),sQuery(id+"F0.wireOp",EDGE,"E3.7.0"),sQuery(id+"F0.wireOp",EDGE,"E4"),sQuery(id+"F0.wireOp",EDGE,"E5.1.0"),sQuery(id+"F0.wireOp",EDGE,"E5.2.0"),sQuery(id+"F0.wireOp",EDGE,"E5.3.0"),sQuery(id+"F0.wireOp",EDGE,"E5.4.0"),sQuery(id+"F0.wireOp",EDGE,"E5.5.0"),sQuery(id+"F0.wireOp",EDGE,"E5.6.0"),sQuery(id+"F0.wireOp",EDGE,"E5.7.0"),sQuery(id+"F0.wireOp",EDGE,"E6")])],"isStart":false});
            var sketch = newSketch(context, id + "F26", { "sketchPlane" : qUnion([Q0])});
            skFitSpline(sketch, "E54", {"points": [v(21, 0) * mm, v(21, 11.6) * mm, v(11.6, 21) * mm, v(0, 21) * mm]});
            skFitSpline(sketch, "E55", {"points": [v(0, 21) * mm, v(-11.6, 21) * mm, v(-21, 11.6) * mm, v(-21, 0) * mm]});
            skFitSpline(sketch, "E56", {"points": [v(-21, 0) * mm, v(-21, -5.57) * mm, v(-18.78, -10.9) * mm, v(-14.85, -14.85) * mm]});
            skFitSpline(sketch, "E57", {"points": [v(-14.85, -14.85) * mm, v(-10.9, -18.78) * mm, v(-5.57, -21) * mm, v(0, -21) * mm]});
            skFitSpline(sketch, "E58", {"points": [v(0, -21) * mm, v(5.57, -21) * mm, v(10.9, -18.78) * mm, v(14.85, -14.85) * mm]});
            skFitSpline(sketch, "E59", {"points": [v(14.85, -14.85) * mm, v(18.78, -10.9) * mm, v(21, -5.57) * mm, v(21, 0) * mm]});
            skLineSegment(sketch, "E60", {"start": v(15.35, 0.04) * mm, "end": v(15.23, 0.9) * mm});
            skLineSegment(sketch, "E61", {"start": v(15.23, 0.9) * mm, "end": v(18, 2.36) * mm});
            skLineSegment(sketch, "E62", {"start": v(18, 2.36) * mm, "end": v(14.95, 3.08) * mm});
            skLineSegment(sketch, "E63", {"start": v(14.95, 3.08) * mm, "end": v(14.84, 3.94) * mm});
            skLineSegment(sketch, "E64", {"start": v(14.84, 3.94) * mm, "end": v(19.1, 4.5) * mm});
            skLineSegment(sketch, "E65", {"start": v(19.1, 4.5) * mm, "end": v(19.18, 3.93) * mm});
            skLineSegment(sketch, "E66", {"start": v(19.18, 3.93) * mm, "end": v(15.43, 3.45) * mm});
            skLineSegment(sketch, "E67", {"start": v(15.43, 3.45) * mm, "end": v(18.5, 2.73) * mm});
            skLineSegment(sketch, "E68", {"start": v(18.5, 2.73) * mm, "end": v(18.58, 2.15) * mm});
            skLineSegment(sketch, "E69", {"start": v(18.58, 2.15) * mm, "end": v(15.8, 0.66) * mm});
            skLineSegment(sketch, "E70", {"start": v(15.8, 0.66) * mm, "end": v(19.54, 1.15) * mm});
            skLineSegment(sketch, "E71", {"start": v(19.54, 1.15) * mm, "end": v(19.61, 0.6) * mm});
            skLineSegment(sketch, "E72", {"start": v(19.61, 0.6) * mm, "end": v(15.35, 0.04) * mm});
            skLineSegment(sketch, "E73", {"start": v(14.6, 4.3) * mm, "end": v(14.43, 4.85) * mm});
            skLineSegment(sketch, "E74", {"start": v(14.43, 4.85) * mm, "end": v(18.54, 6.15) * mm});
            skLineSegment(sketch, "E75", {"start": v(18.54, 6.15) * mm, "end": v(18.72, 5.59) * mm});
            skLineSegment(sketch, "E76", {"start": v(18.72, 5.59) * mm, "end": v(14.6, 4.3) * mm});
            skLineSegment(sketch, "E77", {"start": v(14.35, 5.34) * mm, "end": v(14, 6.04) * mm});
            skLineSegment(sketch, "E78", {"start": v(14, 6.04) * mm, "end": v(16.37, 9.36) * mm});
            skLineSegment(sketch, "E79", {"start": v(16.37, 9.36) * mm, "end": v(13.15, 7.75) * mm});
            skLineSegment(sketch, "E80", {"start": v(13.15, 7.75) * mm, "end": v(12.9, 8.25) * mm});
            skLineSegment(sketch, "E81", {"start": v(12.9, 8.25) * mm, "end": v(16.75, 10.18) * mm});
            skLineSegment(sketch, "E82", {"start": v(16.75, 10.18) * mm, "end": v(17.1, 9.48) * mm});
            skLineSegment(sketch, "E83", {"start": v(17.1, 9.48) * mm, "end": v(14.73, 6.16) * mm});
            skLineSegment(sketch, "E84", {"start": v(14.73, 6.16) * mm, "end": v(17.95, 7.77) * mm});
            skLineSegment(sketch, "E85", {"start": v(17.95, 7.77) * mm, "end": v(18.2, 7.26) * mm});
            skLineSegment(sketch, "E86", {"start": v(18.2, 7.26) * mm, "end": v(14.35, 5.34) * mm});
            skLineSegment(sketch, "E87", {"start": v(12.56, 8.61) * mm, "end": v(12.22, 9.09) * mm});
            skLineSegment(sketch, "E88", {"start": v(12.22, 9.09) * mm, "end": v(15.72, 11.6) * mm});
            skLineSegment(sketch, "E89", {"start": v(15.72, 11.6) * mm, "end": v(16.06, 11.12) * mm});
            skLineSegment(sketch, "E90", {"start": v(16.06, 11.12) * mm, "end": v(12.56, 8.61) * mm});
            skLineSegment(sketch, "E91", {"start": v(9.08, 12.46) * mm, "end": v(9.45, 12.89) * mm});
            skFitSpline(sketch, "E92", {"points": [v(9.45, 12.89) * mm, v(9.55, 12.66) * mm, v(9.66, 12.47) * mm, v(9.77, 12.3) * mm]});
            skFitSpline(sketch, "E93", {"points": [v(9.77, 12.3) * mm, v(9.89, 12.13) * mm, v(10.01, 11.99) * mm, v(10.15, 11.87) * mm]});
            skFitSpline(sketch, "E94", {"points": [v(10.15, 11.87) * mm, v(10.4, 11.66) * mm, v(10.62, 11.55) * mm, v(10.83, 11.53) * mm]});
            skFitSpline(sketch, "E95", {"points": [v(10.83, 11.53) * mm, v(11.04, 11.5) * mm, v(11.22, 11.58) * mm, v(11.36, 11.76) * mm]});
            skFitSpline(sketch, "E96", {"points": [v(11.36, 11.76) * mm, v(11.49, 11.9) * mm, v(11.54, 12.05) * mm, v(11.52, 12.2) * mm]});
            skFitSpline(sketch, "E97", {"points": [v(11.52, 12.2) * mm, v(11.5, 12.34) * mm, v(11.38, 12.54) * mm, v(11.18, 12.8) * mm]});
            skLineSegment(sketch, "E98", {"start": v(11.18, 12.8) * mm, "end": v(10.96, 13.08) * mm});
            skFitSpline(sketch, "E99", {"points": [v(10.96, 13.08) * mm, v(10.69, 13.43) * mm, v(10.54, 13.75) * mm, v(10.52, 14.04) * mm]});
            skFitSpline(sketch, "E100", {"points": [v(10.52, 14.04) * mm, v(10.5, 14.33) * mm, v(10.6, 14.61) * mm, v(10.83, 14.88) * mm]});
            skFitSpline(sketch, "E101", {"points": [v(10.83, 14.88) * mm, v(11.1, 15.2) * mm, v(11.42, 15.34) * mm, v(11.77, 15.32) * mm]});
            skFitSpline(sketch, "E102", {"points": [v(11.77, 15.32) * mm, v(12.12, 15.3) * mm, v(12.5, 15.11) * mm, v(12.91, 14.76) * mm]});
            skFitSpline(sketch, "E103", {"points": [v(12.91, 14.76) * mm, v(13.07, 14.63) * mm, v(13.22, 14.47) * mm, v(13.36, 14.28) * mm]});
            skFitSpline(sketch, "E104", {"points": [v(13.36, 14.28) * mm, v(13.5, 14.1) * mm, v(13.64, 13.89) * mm, v(13.76, 13.66) * mm]});
            skLineSegment(sketch, "E105", {"start": v(13.76, 13.66) * mm, "end": v(13.37, 13.2) * mm});
            skFitSpline(sketch, "E106", {"points": [v(13.37, 13.2) * mm, v(13.28, 13.46) * mm, v(13.17, 13.69) * mm, v(13.04, 13.89) * mm]});
            skFitSpline(sketch, "E107", {"points": [v(13.04, 13.89) * mm, v(12.91, 14.09) * mm, v(12.77, 14.26) * mm, v(12.6, 14.4) * mm]});
            skFitSpline(sketch, "E108", {"points": [v(12.6, 14.4) * mm, v(12.35, 14.62) * mm, v(12.11, 14.74) * mm, v(11.9, 14.76) * mm]});
            skFitSpline(sketch, "E109", {"points": [v(11.9, 14.76) * mm, v(11.67, 14.78) * mm, v(11.48, 14.7) * mm, v(11.32, 14.51) * mm]});
            skFitSpline(sketch, "E110", {"points": [v(11.32, 14.51) * mm, v(11.18, 14.35) * mm, v(11.12, 14.18) * mm, v(11.15, 14) * mm]});
            skFitSpline(sketch, "E111", {"points": [v(11.15, 14) * mm, v(11.16, 13.83) * mm, v(11.27, 13.63) * mm, v(11.45, 13.39) * mm]});
            skLineSegment(sketch, "E112", {"start": v(11.45, 13.39) * mm, "end": v(11.67, 13.1) * mm});
            skFitSpline(sketch, "E113", {"points": [v(11.67, 13.1) * mm, v(11.95, 12.75) * mm, v(12.1, 12.45) * mm, v(12.12, 12.18) * mm]});
            skFitSpline(sketch, "E114", {"points": [v(12.12, 12.18) * mm, v(12.15, 11.91) * mm, v(12.05, 11.66) * mm, v(11.84, 11.4) * mm]});
            skFitSpline(sketch, "E115", {"points": [v(11.84, 11.4) * mm, v(11.59, 11.12) * mm, v(11.3, 10.98) * mm, v(10.95, 10.99) * mm]});
            skFitSpline(sketch, "E116", {"points": [v(10.95, 10.99) * mm, v(10.6, 11) * mm, v(10.25, 11.16) * mm, v(9.9, 11.47) * mm]});
            skFitSpline(sketch, "E117", {"points": [v(9.9, 11.47) * mm, v(9.74, 11.6) * mm, v(9.6, 11.75) * mm, v(9.46, 11.91) * mm]});
            skFitSpline(sketch, "E118", {"points": [v(9.46, 11.91) * mm, v(9.33, 12.08) * mm, v(9.2, 12.26) * mm, v(9.08, 12.46) * mm]});
            skLineSegment(sketch, "E119", {"start": v(8.41, 13.27) * mm, "end": v(9.23, 14.67) * mm});
            skLineSegment(sketch, "E120", {"start": v(9.23, 14.67) * mm, "end": v(8.6, 15.04) * mm});
            skFitSpline(sketch, "E121", {"points": [v(8.6, 15.04) * mm, v(8.36, 15.18) * mm, v(8.14, 15.22) * mm, v(7.94, 15.17) * mm]});
            skFitSpline(sketch, "E122", {"points": [v(7.94, 15.17) * mm, v(7.74, 15.13) * mm, v(7.58, 15) * mm, v(7.45, 14.77) * mm]});
            skFitSpline(sketch, "E123", {"points": [v(7.45, 14.77) * mm, v(7.32, 14.54) * mm, v(7.28, 14.33) * mm, v(7.34, 14.14) * mm]});
            skFitSpline(sketch, "E124", {"points": [v(7.34, 14.14) * mm, v(7.4, 13.94) * mm, v(7.55, 13.78) * mm, v(7.78, 13.64) * mm]});
            skLineSegment(sketch, "E125", {"start": v(7.78, 13.64) * mm, "end": v(8.41, 13.27) * mm});
            skLineSegment(sketch, "E126", {"start": v(8.68, 12.57) * mm, "end": v(7.54, 13.23) * mm});
            skFitSpline(sketch, "E127", {"points": [v(7.54, 13.23) * mm, v(7.12, 13.47) * mm, v(6.86, 13.75) * mm, v(6.76, 14.06) * mm]});
            skFitSpline(sketch, "E128", {"points": [v(6.76, 14.06) * mm, v(6.65, 14.37) * mm, v(6.7, 14.71) * mm, v(6.92, 15.08) * mm]});
            skFitSpline(sketch, "E129", {"points": [v(6.92, 15.08) * mm, v(7.13, 15.44) * mm, v(7.4, 15.66) * mm, v(7.72, 15.72) * mm]});
            skFitSpline(sketch, "E130", {"points": [v(7.72, 15.72) * mm, v(8.05, 15.79) * mm, v(8.42, 15.7) * mm, v(8.83, 15.45) * mm]});
            skLineSegment(sketch, "E131", {"start": v(8.83, 15.45) * mm, "end": v(9.47, 15.09) * mm});
            skLineSegment(sketch, "E132", {"start": v(9.47, 15.09) * mm, "end": v(10.34, 16.58) * mm});
            skLineSegment(sketch, "E133", {"start": v(10.34, 16.58) * mm, "end": v(10.84, 16.29) * mm});
            skLineSegment(sketch, "E134", {"start": v(10.84, 16.29) * mm, "end": v(8.68, 12.57) * mm});
            skLineSegment(sketch, "E135", {"start": v(6.05, 13.97) * mm, "end": v(5.52, 14.2) * mm});
            skLineSegment(sketch, "E136", {"start": v(5.52, 14.2) * mm, "end": v(7.15, 18.18) * mm});
            skLineSegment(sketch, "E137", {"start": v(7.15, 18.18) * mm, "end": v(7.7, 17.95) * mm});
            skLineSegment(sketch, "E138", {"start": v(7.7, 17.95) * mm, "end": v(6.05, 13.97) * mm});
            skLineSegment(sketch, "E139", {"start": v(5.1, 14.44) * mm, "end": v(4.33, 14.62) * mm});
            skLineSegment(sketch, "E140", {"start": v(4.33, 14.62) * mm, "end": v(3.3, 18.57) * mm});
            skLineSegment(sketch, "E141", {"start": v(3.3, 18.57) * mm, "end": v(2.47, 15.06) * mm});
            skLineSegment(sketch, "E142", {"start": v(2.47, 15.06) * mm, "end": v(1.92, 15.19) * mm});
            skLineSegment(sketch, "E143", {"start": v(1.92, 15.19) * mm, "end": v(2.9, 19.38) * mm});
            skLineSegment(sketch, "E144", {"start": v(2.9, 19.38) * mm, "end": v(3.67, 19.2) * mm});
            skLineSegment(sketch, "E145", {"start": v(3.67, 19.2) * mm, "end": v(4.7, 15.26) * mm});
            skLineSegment(sketch, "E146", {"start": v(4.7, 15.26) * mm, "end": v(5.53, 18.76) * mm});
            skLineSegment(sketch, "E147", {"start": v(5.53, 18.76) * mm, "end": v(6.08, 18.63) * mm});
            skLineSegment(sketch, "E148", {"start": v(6.08, 18.63) * mm, "end": v(5.1, 14.44) * mm});
            skLineSegment(sketch, "E149", {"start": v(-0.46, 15.7) * mm, "end": v(-0.57, 17.32) * mm});
            skLineSegment(sketch, "E150", {"start": v(-0.57, 17.32) * mm, "end": v(-1.3, 17.27) * mm});
            skFitSpline(sketch, "E151", {"points": [v(-1.3, 17.27) * mm, v(-1.57, 17.25) * mm, v(-1.77, 17.17) * mm, v(-1.91, 17.02) * mm]});
            skFitSpline(sketch, "E152", {"points": [v(-1.91, 17.02) * mm, v(-2.05, 16.87) * mm, v(-2.1, 16.66) * mm, v(-2.1, 16.4) * mm]});
            skFitSpline(sketch, "E153", {"points": [v(-2.1, 16.4) * mm, v(-2.07, 16.15) * mm, v(-1.99, 15.95) * mm, v(-1.83, 15.82) * mm]});
            skFitSpline(sketch, "E154", {"points": [v(-1.83, 15.82) * mm, v(-1.67, 15.7) * mm, v(-1.46, 15.64) * mm, v(-1.19, 15.66) * mm]});
            skLineSegment(sketch, "E155", {"start": v(-1.19, 15.66) * mm, "end": v(-0.46, 15.7) * mm});
            skLineSegment(sketch, "E156", {"start": v(0.16, 15.27) * mm, "end": v(-1.16, 15.18) * mm});
            skFitSpline(sketch, "E157", {"points": [v(-1.16, 15.18) * mm, v(-1.64, 15.15) * mm, v(-2, 15.23) * mm, v(-2.27, 15.43) * mm]});
            skFitSpline(sketch, "E158", {"points": [v(-2.27, 15.43) * mm, v(-2.53, 15.63) * mm, v(-2.68, 15.94) * mm, v(-2.7, 16.36) * mm]});
            skFitSpline(sketch, "E159", {"points": [v(-2.7, 16.36) * mm, v(-2.73, 16.79) * mm, v(-2.63, 17.11) * mm, v(-2.4, 17.35) * mm]});
            skFitSpline(sketch, "E160", {"points": [v(-2.4, 17.35) * mm, v(-2.17, 17.58) * mm, v(-1.81, 17.71) * mm, v(-1.33, 17.75) * mm]});
            skLineSegment(sketch, "E161", {"start": v(-1.33, 17.75) * mm, "end": v(-0.6, 17.8) * mm});
            skLineSegment(sketch, "E162", {"start": v(-0.6, 17.8) * mm, "end": v(-0.72, 19.52) * mm});
            skLineSegment(sketch, "E163", {"start": v(-0.72, 19.52) * mm, "end": v(-0.14, 19.56) * mm});
            skLineSegment(sketch, "E164", {"start": v(-0.14, 19.56) * mm, "end": v(0.16, 15.27) * mm});
            skFitSpline(sketch, "E165", {"points": [v(-5.13, 16.75) * mm, v(-5.26, 16.76) * mm, v(-5.4, 16.82) * mm, v(-5.55, 16.92) * mm]});
            skFitSpline(sketch, "E166", {"points": [v(-5.55, 16.92) * mm, v(-5.7, 17.02) * mm, v(-5.87, 17.17) * mm, v(-6.05, 17.38) * mm]});
            skLineSegment(sketch, "E167", {"start": v(-6.05, 17.38) * mm, "end": v(-6.93, 18.36) * mm});
            skLineSegment(sketch, "E168", {"start": v(-6.93, 18.36) * mm, "end": v(-6.32, 18.52) * mm});
            skLineSegment(sketch, "E169", {"start": v(-6.32, 18.52) * mm, "end": v(-5.5, 17.6) * mm});
            skFitSpline(sketch, "E170", {"points": [v(-5.5, 17.6) * mm, v(-5.29, 17.36) * mm, v(-5.1, 17.21) * mm, v(-4.95, 17.15) * mm]});
            skFitSpline(sketch, "E171", {"points": [v(-4.95, 17.15) * mm, v(-4.8, 17.1) * mm, v(-4.61, 17.1) * mm, v(-4.39, 17.16) * mm]});
            skLineSegment(sketch, "E172", {"start": v(-4.39, 17.16) * mm, "end": v(-3.78, 17.33) * mm});
            skLineSegment(sketch, "E173", {"start": v(-3.78, 17.33) * mm, "end": v(-4.25, 19.08) * mm});
            skLineSegment(sketch, "E174", {"start": v(-4.25, 19.08) * mm, "end": v(-3.69, 19.23) * mm});
            skLineSegment(sketch, "E175", {"start": v(-3.69, 19.23) * mm, "end": v(-2.56, 15.08) * mm});
            skLineSegment(sketch, "E176", {"start": v(-2.56, 15.08) * mm, "end": v(-3.83, 14.74) * mm});
            skFitSpline(sketch, "E177", {"points": [v(-3.83, 14.74) * mm, v(-4.3, 14.6) * mm, v(-4.69, 14.61) * mm, v(-4.98, 14.75) * mm]});
            skFitSpline(sketch, "E178", {"points": [v(-4.98, 14.75) * mm, v(-5.26, 14.88) * mm, v(-5.46, 15.15) * mm, v(-5.57, 15.55) * mm]});
            skFitSpline(sketch, "E179", {"points": [v(-5.57, 15.55) * mm, v(-5.64, 15.81) * mm, v(-5.64, 16.05) * mm, v(-5.56, 16.25) * mm]});
            skFitSpline(sketch, "E180", {"points": [v(-5.56, 16.25) * mm, v(-5.49, 16.46) * mm, v(-5.35, 16.62) * mm, v(-5.13, 16.75) * mm]});
            skLineSegment(sketch, "E181", {"start": v(-3.25, 15.39) * mm, "end": v(-3.65, 16.86) * mm});
            skLineSegment(sketch, "E182", {"start": v(-3.65, 16.86) * mm, "end": v(-4.36, 16.67) * mm});
            skFitSpline(sketch, "E183", {"points": [v(-4.36, 16.67) * mm, v(-4.63, 16.6) * mm, v(-4.82, 16.48) * mm, v(-4.92, 16.32) * mm]});
            skFitSpline(sketch, "E184", {"points": [v(-4.92, 16.32) * mm, v(-5.02, 16.16) * mm, v(-5.04, 15.95) * mm, v(-4.98, 15.71) * mm]});
            skFitSpline(sketch, "E185", {"points": [v(-4.98, 15.71) * mm, v(-4.91, 15.47) * mm, v(-4.8, 15.3) * mm, v(-4.62, 15.22) * mm]});
            skFitSpline(sketch, "E186", {"points": [v(-4.62, 15.22) * mm, v(-4.45, 15.13) * mm, v(-4.23, 15.12) * mm, v(-3.96, 15.2) * mm]});
            skLineSegment(sketch, "E187", {"start": v(-3.96, 15.2) * mm, "end": v(-3.25, 15.39) * mm});
            skFitSpline(sketch, "E188", {"points": [v(-7.33, 13.79) * mm, v(-6.96, 13.99) * mm, v(-6.74, 14.29) * mm, v(-6.67, 14.68) * mm]});
            skFitSpline(sketch, "E189", {"points": [v(-6.67, 14.68) * mm, v(-6.6, 15.08) * mm, v(-6.69, 15.51) * mm, v(-6.95, 16) * mm]});
            skFitSpline(sketch, "E190", {"points": [v(-6.95, 16) * mm, v(-7.2, 16.47) * mm, v(-7.51, 16.8) * mm, v(-7.88, 16.95) * mm]});
            skFitSpline(sketch, "E191", {"points": [v(-7.88, 16.95) * mm, v(-8.25, 17.11) * mm, v(-8.62, 17.1) * mm, v(-9, 16.9) * mm]});
            skFitSpline(sketch, "E192", {"points": [v(-9, 16.9) * mm, v(-9.36, 16.7) * mm, v(-9.59, 16.4) * mm, v(-9.65, 16) * mm]});
            skFitSpline(sketch, "E193", {"points": [v(-9.65, 16) * mm, v(-9.72, 15.61) * mm, v(-9.63, 15.18) * mm, v(-9.38, 14.7) * mm]});
            skFitSpline(sketch, "E194", {"points": [v(-9.38, 14.7) * mm, v(-9.12, 14.22) * mm, v(-8.8, 13.9) * mm, v(-8.44, 13.73) * mm]});
            skFitSpline(sketch, "E195", {"points": [v(-8.44, 13.73) * mm, v(-8.08, 13.57) * mm, v(-7.7, 13.6) * mm, v(-7.33, 13.79) * mm]});
            skFitSpline(sketch, "E196", {"points": [v(-7.11, 13.37) * mm, v(-7.65, 13.09) * mm, v(-8.17, 13.04) * mm, v(-8.68, 13.23) * mm]});
            skFitSpline(sketch, "E197", {"points": [v(-8.68, 13.23) * mm, v(-9.18, 13.41) * mm, v(-9.6, 13.8) * mm, v(-9.92, 14.4) * mm]});
            skFitSpline(sketch, "E198", {"points": [v(-9.92, 14.4) * mm, v(-10.24, 15) * mm, v(-10.33, 15.57) * mm, v(-10.2, 16.1) * mm]});
            skFitSpline(sketch, "E199", {"points": [v(-10.2, 16.1) * mm, v(-10.08, 16.62) * mm, v(-9.75, 17.03) * mm, v(-9.21, 17.31) * mm]});
            skFitSpline(sketch, "E200", {"points": [v(-9.21, 17.31) * mm, v(-8.68, 17.6) * mm, v(-8.16, 17.65) * mm, v(-7.65, 17.46) * mm]});
            skFitSpline(sketch, "E201", {"points": [v(-7.65, 17.46) * mm, v(-7.14, 17.28) * mm, v(-6.72, 16.88) * mm, v(-6.4, 16.28) * mm]});
            skFitSpline(sketch, "E202", {"points": [v(-6.4, 16.28) * mm, v(-6.08, 15.68) * mm, v(-5.99, 15.12) * mm, v(-6.12, 14.6) * mm]});
            skFitSpline(sketch, "E203", {"points": [v(-6.12, 14.6) * mm, v(-6.25, 14.06) * mm, v(-6.58, 13.66) * mm, v(-7.11, 13.37) * mm]});
            skLineSegment(sketch, "E204", {"start": v(-15.27, 1.45) * mm, "end": v(-15.25, 0.58) * mm});
            skLineSegment(sketch, "E205", {"start": v(-15.25, 0.58) * mm, "end": v(-18.14, -0.62) * mm});
            skLineSegment(sketch, "E206", {"start": v(-18.14, -0.62) * mm, "end": v(-15.17, -1.62) * mm});
            skLineSegment(sketch, "E207", {"start": v(-15.17, -1.62) * mm, "end": v(-15.14, -2.49) * mm});
            skLineSegment(sketch, "E208", {"start": v(-15.14, -2.49) * mm, "end": v(-19.44, -2.63) * mm});
            skLineSegment(sketch, "E209", {"start": v(-19.44, -2.63) * mm, "end": v(-19.46, -2.07) * mm});
            skLineSegment(sketch, "E210", {"start": v(-19.46, -2.07) * mm, "end": v(-15.69, -1.94) * mm});
            skLineSegment(sketch, "E211", {"start": v(-15.69, -1.94) * mm, "end": v(-18.67, -0.93) * mm});
            skLineSegment(sketch, "E212", {"start": v(-18.67, -0.93) * mm, "end": v(-18.7, -0.34) * mm});
            skLineSegment(sketch, "E213", {"start": v(-18.7, -0.34) * mm, "end": v(-15.78, 0.86) * mm});
            skLineSegment(sketch, "E214", {"start": v(-15.78, 0.86) * mm, "end": v(-19.56, 0.74) * mm});
            skLineSegment(sketch, "E215", {"start": v(-19.56, 0.74) * mm, "end": v(-19.58, 1.3) * mm});
            skLineSegment(sketch, "E216", {"start": v(-19.58, 1.3) * mm, "end": v(-15.27, 1.45) * mm});
            skLineSegment(sketch, "E217", {"start": v(-14.95, -2.87) * mm, "end": v(-14.83, -3.44) * mm});
            skLineSegment(sketch, "E218", {"start": v(-14.83, -3.44) * mm, "end": v(-19.04, -4.33) * mm});
            skLineSegment(sketch, "E219", {"start": v(-19.04, -4.33) * mm, "end": v(-19.16, -3.76) * mm});
            skLineSegment(sketch, "E220", {"start": v(-19.16, -3.76) * mm, "end": v(-14.95, -2.87) * mm});
            skLineSegment(sketch, "E221", {"start": v(-14.8, -3.93) * mm, "end": v(-14.52, -4.66) * mm});
            skLineSegment(sketch, "E222", {"start": v(-14.52, -4.66) * mm, "end": v(-17.2, -7.74) * mm});
            skLineSegment(sketch, "E223", {"start": v(-17.2, -7.74) * mm, "end": v(-13.83, -6.45) * mm});
            skLineSegment(sketch, "E224", {"start": v(-13.83, -6.45) * mm, "end": v(-13.63, -6.97) * mm});
            skLineSegment(sketch, "E225", {"start": v(-13.63, -6.97) * mm, "end": v(-17.65, -8.52) * mm});
            skLineSegment(sketch, "E226", {"start": v(-17.65, -8.52) * mm, "end": v(-17.93, -7.78) * mm});
            skLineSegment(sketch, "E227", {"start": v(-17.93, -7.78) * mm, "end": v(-15.25, -4.71) * mm});
            skLineSegment(sketch, "E228", {"start": v(-15.25, -4.71) * mm, "end": v(-18.61, -6) * mm});
            skLineSegment(sketch, "E229", {"start": v(-18.61, -6) * mm, "end": v(-18.81, -5.47) * mm});
            skLineSegment(sketch, "E230", {"start": v(-18.81, -5.47) * mm, "end": v(-14.8, -3.93) * mm});
            skLineSegment(sketch, "E231", {"start": v(-13.33, -7.36) * mm, "end": v(-13.03, -7.86) * mm});
            skLineSegment(sketch, "E232", {"start": v(-13.03, -7.86) * mm, "end": v(-16.76, -10.02) * mm});
            skLineSegment(sketch, "E233", {"start": v(-16.76, -10.02) * mm, "end": v(-17.05, -9.52) * mm});
            skLineSegment(sketch, "E234", {"start": v(-17.05, -9.52) * mm, "end": v(-13.33, -7.36) * mm});
            skLineSegment(sketch, "E235", {"start": v(-10.24, -11.52) * mm, "end": v(-10.65, -11.91) * mm});
            skFitSpline(sketch, "E236", {"points": [v(-10.65, -11.91) * mm, v(-10.72, -11.68) * mm, v(-10.8, -11.47) * mm, v(-10.9, -11.3) * mm]});
            skFitSpline(sketch, "E237", {"points": [v(-10.9, -11.3) * mm, v(-11, -11.12) * mm, v(-11.12, -10.96) * mm, v(-11.24, -10.83) * mm]});
            skFitSpline(sketch, "E238", {"points": [v(-11.24, -10.83) * mm, v(-11.46, -10.6) * mm, v(-11.68, -10.47) * mm, v(-11.88, -10.43) * mm]});
            skFitSpline(sketch, "E239", {"points": [v(-11.88, -10.43) * mm, v(-12.1, -10.39) * mm, v(-12.28, -10.45) * mm, v(-12.44, -10.6) * mm]});
            skFitSpline(sketch, "E240", {"points": [v(-12.44, -10.6) * mm, v(-12.58, -10.73) * mm, v(-12.64, -10.87) * mm, v(-12.64, -11.02) * mm]});
            skFitSpline(sketch, "E241", {"points": [v(-12.64, -11.02) * mm, v(-12.63, -11.17) * mm, v(-12.53, -11.38) * mm, v(-12.36, -11.66) * mm]});
            skLineSegment(sketch, "E242", {"start": v(-12.36, -11.66) * mm, "end": v(-12.17, -11.96) * mm});
            skFitSpline(sketch, "E243", {"points": [v(-12.17, -11.96) * mm, v(-11.93, -12.33) * mm, v(-11.81, -12.67) * mm, v(-11.82, -12.96) * mm]});
            skFitSpline(sketch, "E244", {"points": [v(-11.82, -12.96) * mm, v(-11.83, -13.25) * mm, v(-11.96, -13.52) * mm, v(-12.21, -13.76) * mm]});
            skFitSpline(sketch, "E245", {"points": [v(-12.21, -13.76) * mm, v(-12.51, -14.05) * mm, v(-12.84, -14.17) * mm, v(-13.19, -14.11) * mm]});
            skFitSpline(sketch, "E246", {"points": [v(-13.19, -14.11) * mm, v(-13.54, -14.06) * mm, v(-13.9, -13.84) * mm, v(-14.27, -13.44) * mm]});
            skFitSpline(sketch, "E247", {"points": [v(-14.27, -13.44) * mm, v(-14.4, -13.3) * mm, v(-14.54, -13.12) * mm, v(-14.67, -12.92) * mm]});
            skFitSpline(sketch, "E248", {"points": [v(-14.67, -12.92) * mm, v(-14.8, -12.73) * mm, v(-14.9, -12.5) * mm, v(-15.01, -12.27) * mm]});
            skLineSegment(sketch, "E249", {"start": v(-15.01, -12.27) * mm, "end": v(-14.58, -11.85) * mm});
            skFitSpline(sketch, "E250", {"points": [v(-14.58, -11.85) * mm, v(-14.51, -12.12) * mm, v(-14.42, -12.35) * mm, v(-14.31, -12.56) * mm]});
            skFitSpline(sketch, "E251", {"points": [v(-14.31, -12.56) * mm, v(-14.2, -12.77) * mm, v(-14.08, -12.96) * mm, v(-13.93, -13.12) * mm]});
            skFitSpline(sketch, "E252", {"points": [v(-13.93, -13.12) * mm, v(-13.7, -13.36) * mm, v(-13.47, -13.5) * mm, v(-13.25, -13.54) * mm]});
            skFitSpline(sketch, "E253", {"points": [v(-13.25, -13.54) * mm, v(-13.03, -13.58) * mm, v(-12.84, -13.52) * mm, v(-12.66, -13.35) * mm]});
            skFitSpline(sketch, "E254", {"points": [v(-12.66, -13.35) * mm, v(-12.5, -13.2) * mm, v(-12.43, -13.04) * mm, v(-12.44, -12.87) * mm]});
            skFitSpline(sketch, "E255", {"points": [v(-12.44, -12.87) * mm, v(-12.44, -12.7) * mm, v(-12.52, -12.48) * mm, v(-12.68, -12.22) * mm]});
            skLineSegment(sketch, "E256", {"start": v(-12.68, -12.22) * mm, "end": v(-12.88, -11.92) * mm});
            skFitSpline(sketch, "E257", {"points": [v(-12.88, -11.92) * mm, v(-13.12, -11.54) * mm, v(-13.23, -11.22) * mm, v(-13.23, -10.95) * mm]});
            skFitSpline(sketch, "E258", {"points": [v(-13.23, -10.95) * mm, v(-13.23, -10.68) * mm, v(-13.12, -10.44) * mm, v(-12.88, -10.21) * mm]});
            skFitSpline(sketch, "E259", {"points": [v(-12.88, -10.21) * mm, v(-12.6, -9.95) * mm, v(-12.3, -9.84) * mm, v(-11.95, -9.88) * mm]});
            skFitSpline(sketch, "E260", {"points": [v(-11.95, -9.88) * mm, v(-11.6, -9.92) * mm, v(-11.27, -10.12) * mm, v(-10.95, -10.46) * mm]});
            skFitSpline(sketch, "E261", {"points": [v(-10.95, -10.46) * mm, v(-10.8, -10.6) * mm, v(-10.68, -10.76) * mm, v(-10.56, -10.94) * mm]});
            skFitSpline(sketch, "E262", {"points": [v(-10.56, -10.94) * mm, v(-10.44, -11.12) * mm, v(-10.33, -11.31) * mm, v(-10.24, -11.52) * mm]});
            skLineSegment(sketch, "E263", {"start": v(-9.65, -12.4) * mm, "end": v(-10.59, -13.71) * mm});
            skLineSegment(sketch, "E264", {"start": v(-10.59, -13.71) * mm, "end": v(-10, -14.14) * mm});
            skFitSpline(sketch, "E265", {"points": [v(-10, -14.14) * mm, v(-9.77, -14.3) * mm, v(-9.56, -14.36) * mm, v(-9.36, -14.33) * mm]});
            skFitSpline(sketch, "E266", {"points": [v(-9.36, -14.33) * mm, v(-9.16, -14.3) * mm, v(-8.98, -14.19) * mm, v(-8.83, -13.98) * mm]});
            skFitSpline(sketch, "E267", {"points": [v(-8.83, -13.98) * mm, v(-8.68, -13.77) * mm, v(-8.63, -13.56) * mm, v(-8.66, -13.36) * mm]});
            skFitSpline(sketch, "E268", {"points": [v(-8.66, -13.36) * mm, v(-8.7, -13.16) * mm, v(-8.83, -12.98) * mm, v(-9.05, -12.82) * mm]});
            skLineSegment(sketch, "E269", {"start": v(-9.05, -12.82) * mm, "end": v(-9.65, -12.4) * mm});
            skLineSegment(sketch, "E270", {"start": v(-9.84, -11.67) * mm, "end": v(-8.77, -12.44) * mm});
            skFitSpline(sketch, "E271", {"points": [v(-8.77, -12.44) * mm, v(-8.38, -12.72) * mm, v(-8.15, -13.02) * mm, v(-8.08, -13.34) * mm]});
            skFitSpline(sketch, "E272", {"points": [v(-8.08, -13.34) * mm, v(-8, -13.66) * mm, v(-8.09, -14) * mm, v(-8.33, -14.33) * mm]});
            skFitSpline(sketch, "E273", {"points": [v(-8.33, -14.33) * mm, v(-8.58, -14.68) * mm, v(-8.87, -14.87) * mm, v(-9.2, -14.9) * mm]});
            skFitSpline(sketch, "E274", {"points": [v(-9.2, -14.9) * mm, v(-9.52, -14.93) * mm, v(-9.88, -14.8) * mm, v(-10.27, -14.53) * mm]});
            skLineSegment(sketch, "E275", {"start": v(-10.27, -14.53) * mm, "end": v(-10.87, -14.1) * mm});
            skLineSegment(sketch, "E276", {"start": v(-10.87, -14.1) * mm, "end": v(-11.88, -15.5) * mm});
            skLineSegment(sketch, "E277", {"start": v(-11.88, -15.5) * mm, "end": v(-12.35, -15.16) * mm});
            skLineSegment(sketch, "E278", {"start": v(-12.35, -15.16) * mm, "end": v(-9.84, -11.67) * mm});
            skLineSegment(sketch, "E279", {"start": v(-7.36, -13.32) * mm, "end": v(-6.85, -13.6) * mm});
            skLineSegment(sketch, "E280", {"start": v(-6.85, -13.6) * mm, "end": v(-8.86, -17.4) * mm});
            skLineSegment(sketch, "E281", {"start": v(-8.86, -17.4) * mm, "end": v(-9.38, -17.13) * mm});
            skLineSegment(sketch, "E282", {"start": v(-9.38, -17.13) * mm, "end": v(-7.36, -13.32) * mm});
            skLineSegment(sketch, "E283", {"start": v(-6.45, -13.88) * mm, "end": v(-5.7, -14.14) * mm});
            skLineSegment(sketch, "E284", {"start": v(-5.7, -14.14) * mm, "end": v(-5.06, -18.16) * mm});
            skLineSegment(sketch, "E285", {"start": v(-5.06, -18.16) * mm, "end": v(-3.9, -14.75) * mm});
            skLineSegment(sketch, "E286", {"start": v(-3.9, -14.75) * mm, "end": v(-3.37, -14.93) * mm});
            skLineSegment(sketch, "E287", {"start": v(-3.37, -14.93) * mm, "end": v(-4.76, -19) * mm});
            skLineSegment(sketch, "E288", {"start": v(-4.76, -19) * mm, "end": v(-5.5, -18.75) * mm});
            skLineSegment(sketch, "E289", {"start": v(-5.5, -18.75) * mm, "end": v(-6.14, -14.73) * mm});
            skLineSegment(sketch, "E290", {"start": v(-6.14, -14.73) * mm, "end": v(-7.3, -18.14) * mm});
            skLineSegment(sketch, "E291", {"start": v(-7.3, -18.14) * mm, "end": v(-7.84, -17.96) * mm});
            skLineSegment(sketch, "E292", {"start": v(-7.84, -17.96) * mm, "end": v(-6.45, -13.88) * mm});
            skLineSegment(sketch, "E293", {"start": v(-1.06, -15.67) * mm, "end": v(-1.1, -17.29) * mm});
            skLineSegment(sketch, "E294", {"start": v(-1.1, -17.29) * mm, "end": v(-0.37, -17.3) * mm});
            skFitSpline(sketch, "E295", {"points": [v(-0.37, -17.3) * mm, v(-0.1, -17.32) * mm, v(0.11, -17.25) * mm, v(0.27, -17.12) * mm]});
            skFitSpline(sketch, "E296", {"points": [v(0.27, -17.12) * mm, v(0.42, -16.98) * mm, v(0.5, -16.78) * mm, v(0.5, -16.52) * mm]});
            skFitSpline(sketch, "E297", {"points": [v(0.5, -16.52) * mm, v(0.51, -16.27) * mm, v(0.44, -16.06) * mm, v(0.3, -15.92) * mm]});
            skFitSpline(sketch, "E298", {"points": [v(0.3, -15.92) * mm, v(0.15, -15.78) * mm, v(-0.05, -15.7) * mm, v(-0.32, -15.7) * mm]});
            skLineSegment(sketch, "E299", {"start": v(-0.32, -15.7) * mm, "end": v(-1.06, -15.67) * mm});
            skLineSegment(sketch, "E300", {"start": v(-1.63, -15.18) * mm, "end": v(-0.31, -15.21) * mm});
            skFitSpline(sketch, "E301", {"points": [v(-0.31, -15.21) * mm, v(0.17, -15.23) * mm, v(0.53, -15.35) * mm, v(0.77, -15.57) * mm]});
            skFitSpline(sketch, "E302", {"points": [v(0.77, -15.57) * mm, v(1.01, -15.8) * mm, v(1.13, -16.12) * mm, v(1.12, -16.54) * mm]});
            skFitSpline(sketch, "E303", {"points": [v(1.12, -16.54) * mm, v(1.1, -16.96) * mm, v(0.97, -17.28) * mm, v(0.72, -17.5) * mm]});
            skFitSpline(sketch, "E304", {"points": [v(0.72, -17.5) * mm, v(0.47, -17.7) * mm, v(0.1, -17.8) * mm, v(-0.38, -17.79) * mm]});
            skLineSegment(sketch, "E305", {"start": v(-0.38, -17.79) * mm, "end": v(-1.11, -17.77) * mm});
            skLineSegment(sketch, "E306", {"start": v(-1.11, -17.77) * mm, "end": v(-1.16, -19.5) * mm});
            skLineSegment(sketch, "E307", {"start": v(-1.16, -19.5) * mm, "end": v(-1.74, -19.48) * mm});
            skLineSegment(sketch, "E308", {"start": v(-1.74, -19.48) * mm, "end": v(-1.63, -15.18) * mm});
            skLineSegment(sketch, "E309", {"start": v(-1.63, -15.18) * mm, "end": v(-1.63, -15.18) * mm});
            skFitSpline(sketch, "E310", {"points": [v(3.5, -17.16) * mm, v(3.63, -17.18) * mm, v(3.77, -17.25) * mm, v(3.9, -17.37) * mm]});
            skFitSpline(sketch, "E311", {"points": [v(3.9, -17.37) * mm, v(4.05, -17.49) * mm, v(4.2, -17.65) * mm, v(4.35, -17.87) * mm]});
            skLineSegment(sketch, "E312", {"start": v(4.35, -17.87) * mm, "end": v(5.13, -18.93) * mm});
            skLineSegment(sketch, "E313", {"start": v(5.13, -18.93) * mm, "end": v(4.51, -19.04) * mm});
            skLineSegment(sketch, "E314", {"start": v(4.51, -19.04) * mm, "end": v(3.79, -18.04) * mm});
            skFitSpline(sketch, "E315", {"points": [v(3.79, -18.04) * mm, v(3.6, -17.78) * mm, v(3.43, -17.62) * mm, v(3.28, -17.54) * mm]});
            skFitSpline(sketch, "E316", {"points": [v(3.28, -17.54) * mm, v(3.14, -17.47) * mm, v(2.95, -17.46) * mm, v(2.72, -17.5) * mm]});
            skLineSegment(sketch, "E317", {"start": v(2.72, -17.5) * mm, "end": v(2.1, -17.6) * mm});
            skLineSegment(sketch, "E318", {"start": v(2.1, -17.6) * mm, "end": v(2.4, -19.4) * mm});
            skLineSegment(sketch, "E319", {"start": v(2.4, -19.4) * mm, "end": v(1.83, -19.5) * mm});
            skLineSegment(sketch, "E320", {"start": v(1.83, -19.5) * mm, "end": v(1.1, -15.25) * mm});
            skLineSegment(sketch, "E321", {"start": v(1.1, -15.25) * mm, "end": v(2.4, -15.03) * mm});
            skFitSpline(sketch, "E322", {"points": [v(2.4, -15.03) * mm, v(2.89, -14.95) * mm, v(3.27, -14.99) * mm, v(3.54, -15.15) * mm]});
            skFitSpline(sketch, "E323", {"points": [v(3.54, -15.15) * mm, v(3.81, -15.31) * mm, v(3.99, -15.6) * mm, v(4.05, -16) * mm]});
            skFitSpline(sketch, "E324", {"points": [v(4.05, -16) * mm, v(4.1, -16.27) * mm, v(4.07, -16.5) * mm, v(3.98, -16.7) * mm]});
            skFitSpline(sketch, "E325", {"points": [v(3.98, -16.7) * mm, v(3.89, -16.9) * mm, v(3.73, -17.05) * mm, v(3.5, -17.16) * mm]});
            skLineSegment(sketch, "E326", {"start": v(1.76, -15.62) * mm, "end": v(2.02, -17.13) * mm});
            skLineSegment(sketch, "E327", {"start": v(2.02, -17.13) * mm, "end": v(2.74, -17) * mm});
            skFitSpline(sketch, "E328", {"points": [v(2.74, -17) * mm, v(3.01, -16.96) * mm, v(3.21, -16.86) * mm, v(3.33, -16.71) * mm]});
            skFitSpline(sketch, "E329", {"points": [v(3.33, -16.71) * mm, v(3.45, -16.56) * mm, v(3.5, -16.36) * mm, v(3.45, -16.11) * mm]});
            skFitSpline(sketch, "E330", {"points": [v(3.45, -16.11) * mm, v(3.4, -15.86) * mm, v(3.3, -15.69) * mm, v(3.14, -15.59) * mm]});
            skFitSpline(sketch, "E331", {"points": [v(3.14, -15.59) * mm, v(2.98, -15.48) * mm, v(2.76, -15.45) * mm, v(2.48, -15.5) * mm]});
            skLineSegment(sketch, "E332", {"start": v(2.48, -15.5) * mm, "end": v(1.76, -15.62) * mm});
            skFitSpline(sketch, "E333", {"points": [v(5.98, -14.43) * mm, v(5.59, -14.59) * mm, v(5.34, -14.86) * mm, v(5.23, -15.25) * mm]});
            skFitSpline(sketch, "E334", {"points": [v(5.23, -15.25) * mm, v(5.12, -15.64) * mm, v(5.17, -16.08) * mm, v(5.38, -16.58) * mm]});
            skFitSpline(sketch, "E335", {"points": [v(5.38, -16.58) * mm, v(5.59, -17.08) * mm, v(5.87, -17.43) * mm, v(6.22, -17.63) * mm]});
            skFitSpline(sketch, "E336", {"points": [v(6.22, -17.63) * mm, v(6.57, -17.82) * mm, v(6.94, -17.84) * mm, v(7.33, -17.68) * mm]});
            skFitSpline(sketch, "E337", {"points": [v(7.33, -17.68) * mm, v(7.72, -17.52) * mm, v(7.97, -17.24) * mm, v(8.07, -16.86) * mm]});
            skFitSpline(sketch, "E338", {"points": [v(8.07, -16.86) * mm, v(8.18, -16.47) * mm, v(8.13, -16.03) * mm, v(7.93, -15.53) * mm]});
            skFitSpline(sketch, "E339", {"points": [v(7.93, -15.53) * mm, v(7.72, -15.03) * mm, v(7.44, -14.68) * mm, v(7.09, -14.48) * mm]});
            skFitSpline(sketch, "E340", {"points": [v(7.09, -14.48) * mm, v(6.74, -14.28) * mm, v(6.37, -14.27) * mm, v(5.98, -14.43) * mm]});
            skFitSpline(sketch, "E341", {"points": [v(5.8, -14) * mm, v(6.36, -13.76) * mm, v(6.88, -13.76) * mm, v(7.37, -14) * mm]});
            skFitSpline(sketch, "E342", {"points": [v(7.37, -14) * mm, v(7.86, -14.23) * mm, v(8.23, -14.66) * mm, v(8.5, -15.3) * mm]});
            skFitSpline(sketch, "E343", {"points": [v(8.5, -15.3) * mm, v(8.75, -15.92) * mm, v(8.8, -16.49) * mm, v(8.61, -17) * mm]});
            skFitSpline(sketch, "E344", {"points": [v(8.61, -17) * mm, v(8.44, -17.51) * mm, v(8.07, -17.88) * mm, v(7.5, -18.12) * mm]});
            skFitSpline(sketch, "E345", {"points": [v(7.5, -18.12) * mm, v(6.95, -18.35) * mm, v(6.43, -18.35) * mm, v(5.94, -18.11) * mm]});
            skFitSpline(sketch, "E346", {"points": [v(5.94, -18.11) * mm, v(5.45, -17.88) * mm, v(5.07, -17.45) * mm, v(4.81, -16.82) * mm]});
            skFitSpline(sketch, "E347", {"points": [v(4.81, -16.82) * mm, v(4.55, -16.19) * mm, v(4.51, -15.62) * mm, v(4.69, -15.1) * mm]});
            skFitSpline(sketch, "E348", {"points": [v(4.69, -15.1) * mm, v(4.87, -14.6) * mm, v(5.24, -14.22) * mm, v(5.8, -14) * mm]});
            skLineSegment(sketch, "E349", {"start": v(5.8, -14) * mm, "end": v(5.8, -14) * mm});
            skSolve(sketch);
        }
        {
            var Q0;
            Q0=makeQuery(id+"F26.imprint","IMPRINT",FACE,{"disambiguationData":[TD([[makeQuery(id+"F26.imprint","IMPRINT",EDGE,{"derivedFrom":sQuery(id+"F26.wireOp",EDGE,"E188")}),-1.0]])]});
            var Q1;
            Q1=makeQuery(id+"F26.imprint","IMPRINT",FACE,{"disambiguationData":[TD([[makeQuery(id+"F26.imprint","IMPRINT",EDGE,{"derivedFrom":sQuery(id+"F26.wireOp",EDGE,"E165")}),-1.0]])]});
            var Q2;
            Q2=makeQuery(id+"F26.imprint","IMPRINT",FACE,{"disambiguationData":[TD([[makeQuery(id+"F26.imprint","IMPRINT",EDGE,{"derivedFrom":sQuery(id+"F26.wireOp",EDGE,"E149")}),-1.0]])]});
            var Q3;
            {var subQ0=sQuery(id+"F26.wireOp",EDGE,"E203");var subQ1=sQuery(id+"F26.wireOp",EDGE,"E196");var subQ2=makeQuery(id+"F26.imprint","INTERSECT",VERTEX,{"derivedFrom":[subQ1,subQ0]});Q3=makeQuery(id+"F26.imprint","IMPRINT",FACE,{"disambiguationData":[TD([[makeQuery(id+"F26.imprint","IMPRINT",EDGE,{"disambiguationData":[TD([[subQ2,-1.0]])],"derivedFrom":subQ1}),-1.0]])]});}
            var Q4;
            {var subQ0=sQuery(id+"F26.wireOp",EDGE,"E176");Q4=makeQuery(id+"F26.imprint","IMPRINT",FACE,{"disambiguationData":[TD([[makeQuery(id+"F26.imprint","IMPRINT",EDGE,{"derivedFrom":subQ0}),-1.0]])]});}
            var Q5;
            {var subQ0=sQuery(id+"F26.wireOp",EDGE,"E156");Q5=makeQuery(id+"F26.imprint","IMPRINT",FACE,{"disambiguationData":[TD([[makeQuery(id+"F26.imprint","IMPRINT",EDGE,{"derivedFrom":subQ0}),-1.0]])]});}
            var Q6;
            {var subQ0=sQuery(id+"F26.wireOp",EDGE,"E142");Q6=makeQuery(id+"F26.imprint","IMPRINT",FACE,{"disambiguationData":[TD([[makeQuery(id+"F26.imprint","IMPRINT",EDGE,{"derivedFrom":subQ0}),-1.0]])]});}
            var Q7;
            {var subQ0=sQuery(id+"F26.wireOp",EDGE,"E139");Q7=makeQuery(id+"F26.imprint","IMPRINT",FACE,{"disambiguationData":[TD([[makeQuery(id+"F26.imprint","IMPRINT",EDGE,{"derivedFrom":subQ0}),-1.0]])]});}
            var Q8;
            {var subQ0=sQuery(id+"F26.wireOp",EDGE,"E144");Q8=makeQuery(id+"F26.imprint","IMPRINT",FACE,{"disambiguationData":[TD([[makeQuery(id+"F26.imprint","IMPRINT",EDGE,{"derivedFrom":subQ0}),-1.0]])]});}
            var Q9;
            {var subQ0=sQuery(id+"F26.wireOp",EDGE,"E135");Q9=makeQuery(id+"F26.imprint","IMPRINT",FACE,{"disambiguationData":[TD([[makeQuery(id+"F26.imprint","IMPRINT",EDGE,{"derivedFrom":subQ0}),-1.0]])]});}
            var Q10;
            {var subQ0=sQuery(id+"F26.wireOp",EDGE,"E137");Q10=makeQuery(id+"F26.imprint","IMPRINT",FACE,{"disambiguationData":[TD([[makeQuery(id+"F26.imprint","IMPRINT",EDGE,{"derivedFrom":subQ0}),-1.0]])]});}
            var Q11;
            {var subQ0=sQuery(id+"F26.wireOp",EDGE,"E126");Q11=makeQuery(id+"F26.imprint","IMPRINT",FACE,{"disambiguationData":[TD([[makeQuery(id+"F26.imprint","IMPRINT",EDGE,{"derivedFrom":subQ0}),-1.0]])]});}
            var Q12;
            Q12=makeQuery(id+"F26.imprint","IMPRINT",FACE,{"disambiguationData":[TD([[makeQuery(id+"F26.imprint","IMPRINT",EDGE,{"derivedFrom":sQuery(id+"F26.wireOp",EDGE,"E119")}),-1.0]])]});
            var Q13;
            {var subQ0=sQuery(id+"F26.wireOp",EDGE,"E117");Q13=makeQuery(id+"F26.imprint","IMPRINT",FACE,{"disambiguationData":[TD([[makeQuery(id+"F26.imprint","IMPRINT",EDGE,{"derivedFrom":subQ0}),-1.0]])]});}
            var Q14;
            {var subQ0=sQuery(id+"F26.wireOp",EDGE,"E91");Q14=makeQuery(id+"F26.imprint","IMPRINT",FACE,{"disambiguationData":[TD([[makeQuery(id+"F26.imprint","IMPRINT",EDGE,{"derivedFrom":subQ0}),-1.0]])]});}
            var Q15;
            {var subQ0=sQuery(id+"F26.wireOp",EDGE,"E89");Q15=makeQuery(id+"F26.imprint","IMPRINT",FACE,{"disambiguationData":[TD([[makeQuery(id+"F26.imprint","IMPRINT",EDGE,{"derivedFrom":subQ0}),-1.0]])]});}
            var Q16;
            {var subQ0=sQuery(id+"F26.wireOp",EDGE,"E87");Q16=makeQuery(id+"F26.imprint","IMPRINT",FACE,{"disambiguationData":[TD([[makeQuery(id+"F26.imprint","IMPRINT",EDGE,{"derivedFrom":subQ0}),-1.0]])]});}
            var Q17;
            {var subQ0=sQuery(id+"F26.wireOp",EDGE,"E80");Q17=makeQuery(id+"F26.imprint","IMPRINT",FACE,{"disambiguationData":[TD([[makeQuery(id+"F26.imprint","IMPRINT",EDGE,{"derivedFrom":subQ0}),-1.0]])]});}
            var Q18;
            {var subQ0=sQuery(id+"F26.wireOp",EDGE,"E82");Q18=makeQuery(id+"F26.imprint","IMPRINT",FACE,{"disambiguationData":[TD([[makeQuery(id+"F26.imprint","IMPRINT",EDGE,{"derivedFrom":subQ0}),-1.0]])]});}
            var Q19;
            {var subQ0=sQuery(id+"F26.wireOp",EDGE,"E75");Q19=makeQuery(id+"F26.imprint","IMPRINT",FACE,{"disambiguationData":[TD([[makeQuery(id+"F26.imprint","IMPRINT",EDGE,{"derivedFrom":subQ0}),-1.0]])]});}
            var Q20;
            {var subQ0=sQuery(id+"F26.wireOp",EDGE,"E73");Q20=makeQuery(id+"F26.imprint","IMPRINT",FACE,{"disambiguationData":[TD([[makeQuery(id+"F26.imprint","IMPRINT",EDGE,{"derivedFrom":subQ0}),-1.0]])]});}
            var Q21;
            {var subQ6=sQuery(id+"F26.wireOp",EDGE,"E65");Q21=makeQuery(id+"F26.imprint","IMPRINT",FACE,{"disambiguationData":[TD([[makeQuery(id+"F26.imprint","IMPRINT",EDGE,{"derivedFrom":subQ6}),-1.0]])]});}
            var Q22;
            {var subQ0=sQuery(id+"F26.wireOp",EDGE,"E63");Q22=makeQuery(id+"F26.imprint","IMPRINT",FACE,{"disambiguationData":[TD([[makeQuery(id+"F26.imprint","IMPRINT",EDGE,{"derivedFrom":subQ0}),-1.0]])]});}
            var Q23;
            {var subQ0=sQuery(id+"F26.wireOp",EDGE,"E60");Q23=makeQuery(id+"F26.imprint","IMPRINT",FACE,{"disambiguationData":[TD([[makeQuery(id+"F26.imprint","IMPRINT",EDGE,{"derivedFrom":subQ0}),-1.0]])]});}
            var Q24;
            {var subQ0=sQuery(id+"F26.wireOp",EDGE,"E77");Q24=makeQuery(id+"F26.imprint","IMPRINT",FACE,{"disambiguationData":[TD([[makeQuery(id+"F26.imprint","IMPRINT",EDGE,{"derivedFrom":subQ0}),-1.0]])]});}
            var Q25;
            Q25=makeQuery(id+"F26.imprint","IMPRINT",FACE,{"disambiguationData":[TD([[makeQuery(id+"F26.imprint","IMPRINT",EDGE,{"derivedFrom":sQuery(id+"F26.wireOp",EDGE,"E333")}),-1.0]])]});
            var Q26;
            {var subQ0=sQuery(id+"F26.wireOp",EDGE,"E348");var subQ1=sQuery(id+"F26.wireOp",EDGE,"E341");var subQ2=makeQuery(id+"F26.imprint","INTERSECT",VERTEX,{"derivedFrom":[subQ1,subQ0]});Q26=makeQuery(id+"F26.imprint","IMPRINT",FACE,{"disambiguationData":[TD([[makeQuery(id+"F26.imprint","IMPRINT",EDGE,{"disambiguationData":[TD([[subQ2,-1.0]])],"derivedFrom":subQ1}),-1.0]])]});}
            var Q27;
            Q27=makeQuery(id+"F26.imprint","IMPRINT",FACE,{"disambiguationData":[TD([[makeQuery(id+"F26.imprint","IMPRINT",EDGE,{"derivedFrom":sQuery(id+"F26.wireOp",EDGE,"E310")}),-1.0]])]});
            var Q28;
            {var subQ0=sQuery(id+"F26.wireOp",EDGE,"E321");Q28=makeQuery(id+"F26.imprint","IMPRINT",FACE,{"disambiguationData":[TD([[makeQuery(id+"F26.imprint","IMPRINT",EDGE,{"derivedFrom":subQ0}),-1.0]])]});}
            var Q29;
            Q29=makeQuery(id+"F26.imprint","IMPRINT",FACE,{"disambiguationData":[TD([[makeQuery(id+"F26.imprint","IMPRINT",EDGE,{"derivedFrom":sQuery(id+"F26.wireOp",EDGE,"E293")}),-1.0]])]});
            var Q30;
            {var subQ0=sQuery(id+"F26.wireOp",EDGE,"E300");Q30=makeQuery(id+"F26.imprint","IMPRINT",FACE,{"disambiguationData":[TD([[makeQuery(id+"F26.imprint","IMPRINT",EDGE,{"derivedFrom":subQ0}),-1.0]])]});}
            var Q31;
            {var subQ0=sQuery(id+"F26.wireOp",EDGE,"E288");Q31=makeQuery(id+"F26.imprint","IMPRINT",FACE,{"disambiguationData":[TD([[makeQuery(id+"F26.imprint","IMPRINT",EDGE,{"derivedFrom":subQ0}),-1.0]])]});}
            var Q32;
            {var subQ0=sQuery(id+"F26.wireOp",EDGE,"E286");Q32=makeQuery(id+"F26.imprint","IMPRINT",FACE,{"disambiguationData":[TD([[makeQuery(id+"F26.imprint","IMPRINT",EDGE,{"derivedFrom":subQ0}),-1.0]])]});}
            var Q33;
            {var subQ0=sQuery(id+"F26.wireOp",EDGE,"E283");Q33=makeQuery(id+"F26.imprint","IMPRINT",FACE,{"disambiguationData":[TD([[makeQuery(id+"F26.imprint","IMPRINT",EDGE,{"derivedFrom":subQ0}),-1.0]])]});}
            var Q34;
            {var subQ0=sQuery(id+"F26.wireOp",EDGE,"E281");Q34=makeQuery(id+"F26.imprint","IMPRINT",FACE,{"disambiguationData":[TD([[makeQuery(id+"F26.imprint","IMPRINT",EDGE,{"derivedFrom":subQ0}),-1.0]])]});}
            var Q35;
            {var subQ0=sQuery(id+"F26.wireOp",EDGE,"E279");Q35=makeQuery(id+"F26.imprint","IMPRINT",FACE,{"disambiguationData":[TD([[makeQuery(id+"F26.imprint","IMPRINT",EDGE,{"derivedFrom":subQ0}),-1.0]])]});}
            var Q36;
            Q36=makeQuery(id+"F26.imprint","IMPRINT",FACE,{"disambiguationData":[TD([[makeQuery(id+"F26.imprint","IMPRINT",EDGE,{"derivedFrom":sQuery(id+"F26.wireOp",EDGE,"E263")}),-1.0]])]});
            var Q37;
            {var subQ0=sQuery(id+"F26.wireOp",EDGE,"E235");Q37=makeQuery(id+"F26.imprint","IMPRINT",FACE,{"disambiguationData":[TD([[makeQuery(id+"F26.imprint","IMPRINT",EDGE,{"derivedFrom":subQ0}),-1.0]])]});}
            var Q38;
            {var subQ0=sQuery(id+"F26.wireOp",EDGE,"E261");Q38=makeQuery(id+"F26.imprint","IMPRINT",FACE,{"disambiguationData":[TD([[makeQuery(id+"F26.imprint","IMPRINT",EDGE,{"derivedFrom":subQ0}),-1.0]])]});}
            var Q39;
            {var subQ0=sQuery(id+"F26.wireOp",EDGE,"E233");Q39=makeQuery(id+"F26.imprint","IMPRINT",FACE,{"disambiguationData":[TD([[makeQuery(id+"F26.imprint","IMPRINT",EDGE,{"derivedFrom":subQ0}),-1.0]])]});}
            var Q40;
            {var subQ0=sQuery(id+"F26.wireOp",EDGE,"E226");Q40=makeQuery(id+"F26.imprint","IMPRINT",FACE,{"disambiguationData":[TD([[makeQuery(id+"F26.imprint","IMPRINT",EDGE,{"derivedFrom":subQ0}),-1.0]])]});}
            var Q41;
            {var subQ0=sQuery(id+"F26.wireOp",EDGE,"E224");Q41=makeQuery(id+"F26.imprint","IMPRINT",FACE,{"disambiguationData":[TD([[makeQuery(id+"F26.imprint","IMPRINT",EDGE,{"derivedFrom":subQ0}),-1.0]])]});}
            var Q42;
            {var subQ0=sQuery(id+"F26.wireOp",EDGE,"E231");Q42=makeQuery(id+"F26.imprint","IMPRINT",FACE,{"disambiguationData":[TD([[makeQuery(id+"F26.imprint","IMPRINT",EDGE,{"derivedFrom":subQ0}),-1.0]])]});}
            var Q43;
            {var subQ0=sQuery(id+"F26.wireOp",EDGE,"E221");Q43=makeQuery(id+"F26.imprint","IMPRINT",FACE,{"disambiguationData":[TD([[makeQuery(id+"F26.imprint","IMPRINT",EDGE,{"derivedFrom":subQ0}),-1.0]])]});}
            var Q44;
            {var subQ0=sQuery(id+"F26.wireOp",EDGE,"E219");Q44=makeQuery(id+"F26.imprint","IMPRINT",FACE,{"disambiguationData":[TD([[makeQuery(id+"F26.imprint","IMPRINT",EDGE,{"derivedFrom":subQ0}),-1.0]])]});}
            var Q45;
            {var subQ0=sQuery(id+"F26.wireOp",EDGE,"E217");Q45=makeQuery(id+"F26.imprint","IMPRINT",FACE,{"disambiguationData":[TD([[makeQuery(id+"F26.imprint","IMPRINT",EDGE,{"derivedFrom":subQ0}),-1.0]])]});}
            var Q46;
            {var subQ6=sQuery(id+"F26.wireOp",EDGE,"E209");Q46=makeQuery(id+"F26.imprint","IMPRINT",FACE,{"disambiguationData":[TD([[makeQuery(id+"F26.imprint","IMPRINT",EDGE,{"derivedFrom":subQ6}),-1.0]])]});}
            var Q47;
            {var subQ0=sQuery(id+"F26.wireOp",EDGE,"E207");Q47=makeQuery(id+"F26.imprint","IMPRINT",FACE,{"disambiguationData":[TD([[makeQuery(id+"F26.imprint","IMPRINT",EDGE,{"derivedFrom":subQ0}),-1.0]])]});}
            var Q48;
            {var subQ0=sQuery(id+"F26.wireOp",EDGE,"E204");Q48=makeQuery(id+"F26.imprint","IMPRINT",FACE,{"disambiguationData":[TD([[makeQuery(id+"F26.imprint","IMPRINT",EDGE,{"derivedFrom":subQ0}),-1.0]])]});}
            extrude(context, id + "F27", {"entities" : qUnion([Q0, Q1, Q2, Q3, Q4, Q5, Q6, Q7, Q8, Q9, Q10, Q11, Q12, Q13, Q14, Q15, Q16, Q17, Q18, Q19, Q20, Q21, Q22, Q23, Q24, Q25, Q26, Q27, Q28, Q29, Q30, Q31, Q32, Q33, Q34, Q35, Q36, Q37, Q38, Q39, Q40, Q41, Q42, Q43, Q44, Q45, Q46, Q47, Q48]), "operationType" : NewBodyOperationType.ADD, "depth" : 1 * mm});
        }
    });
